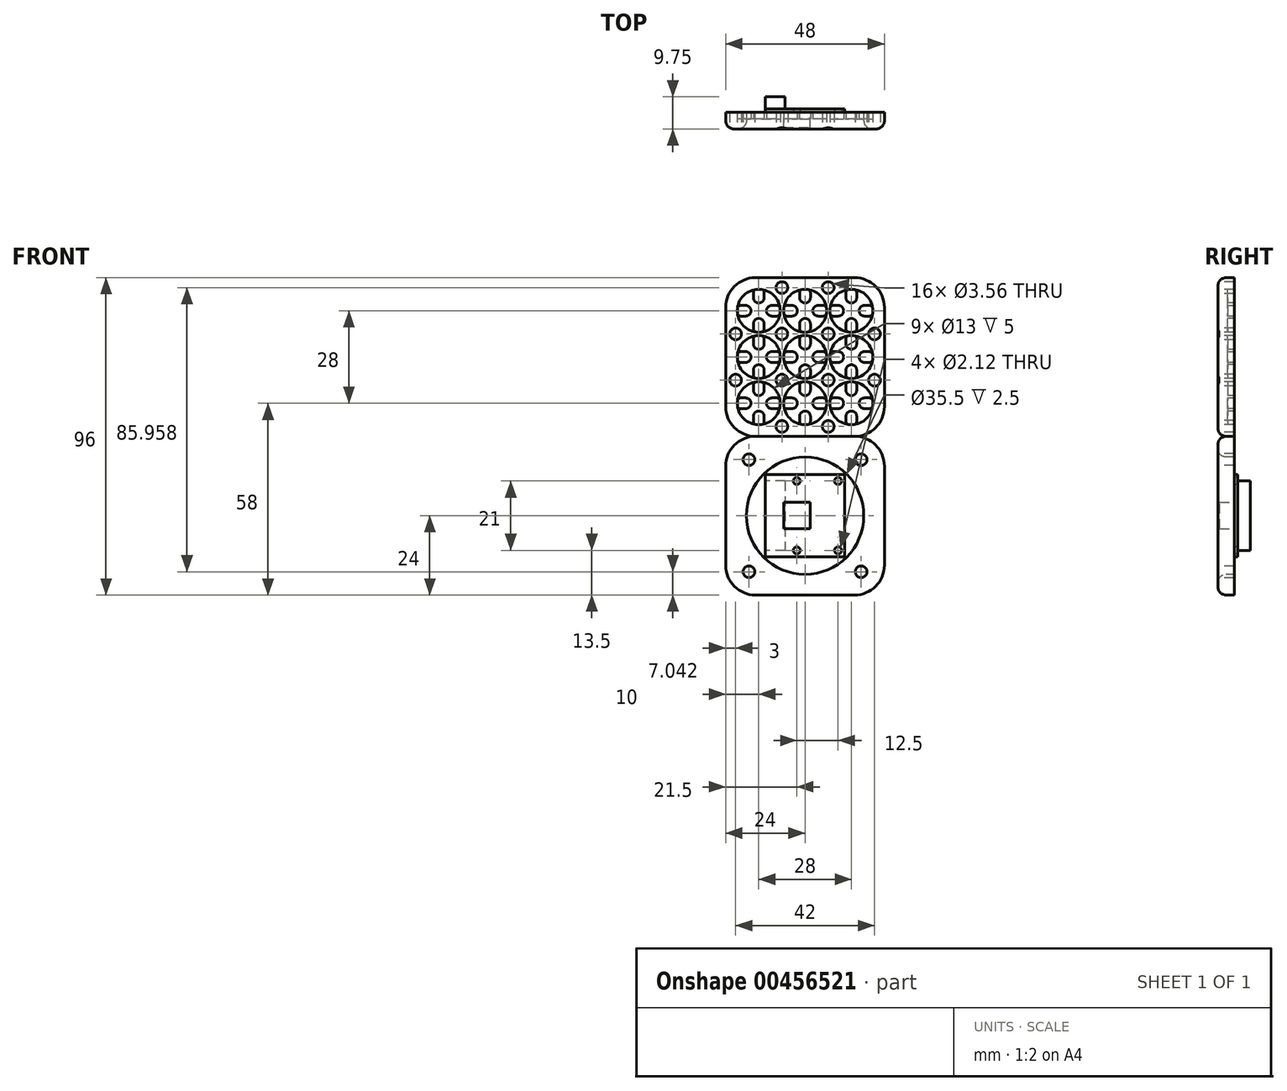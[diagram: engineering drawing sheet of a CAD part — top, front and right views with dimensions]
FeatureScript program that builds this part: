
annotation { "Feature Type Name" : "Feature", "Feature Type Description" : "" }
export const myFeature = defineFeature(function(context is Context, id is Id, definition is map)
    precondition{}
    {
        {
            var Q0;
            Q0=qCreatedBy(makeId("Front.planeOp"),FACE);
            var sketch = newSketch(context, id + "F0", { "sketchPlane" : qUnion([Q0])});
            skCircle(sketch, "E0", {"center": v(0, 0) * mm, "radius": 6.5 * mm});
            skCircle(sketch, "E1", {"center": v(0, 0) * mm, "radius": 7 * mm, "construction": true});
            skLineSegment(sketch, "E2", {"start": v(0, 7) * mm, "end": v(0, 14) * mm, "construction": true});
            skCircle(sketch, "E3", {"center": v(0, 14) * mm, "radius": 7 * mm, "construction": true});
            skCircle(sketch, "E4", {"center": v(0, 14) * mm, "radius": 6.5 * mm});
            skLineSegment(sketch, "E5", {"start": v(0, -7) * mm, "end": v(0, -14) * mm, "construction": true});
            skCircle(sketch, "E6", {"center": v(0, -14) * mm, "radius": 7 * mm, "construction": true});
            skCircle(sketch, "E7", {"center": v(0, -14) * mm, "radius": 6.5 * mm});
            skLineSegment(sketch, "E8", {"start": v(-7, 14) * mm, "end": v(-14, 14) * mm, "construction": true});
            skLineSegment(sketch, "E9", {"start": v(-7, 0) * mm, "end": v(-14, 0) * mm, "construction": true});
            skLineSegment(sketch, "E10", {"start": v(-7, -14) * mm, "end": v(-14, -14) * mm, "construction": true});
            skLineSegment(sketch, "E11", {"start": v(7, 14) * mm, "end": v(14, 14) * mm, "construction": true});
            skLineSegment(sketch, "E12", {"start": v(7, 0) * mm, "end": v(14, 0) * mm, "construction": true});
            skLineSegment(sketch, "E13", {"start": v(7, -14) * mm, "end": v(14, -14) * mm, "construction": true});
            skCircle(sketch, "E14", {"center": v(14, 14) * mm, "radius": 7 * mm, "construction": true});
            skCircle(sketch, "E15", {"center": v(14, 0) * mm, "radius": 7 * mm, "construction": true});
            skCircle(sketch, "E16", {"center": v(14, -14) * mm, "radius": 7 * mm, "construction": true});
            skCircle(sketch, "E17", {"center": v(-14, -14) * mm, "radius": 7 * mm, "construction": true});
            skCircle(sketch, "E18", {"center": v(-14, 0) * mm, "radius": 7 * mm, "construction": true});
            skCircle(sketch, "E19", {"center": v(-14, 14) * mm, "radius": 7 * mm, "construction": true});
            skCircle(sketch, "E20", {"center": v(-14, 14) * mm, "radius": 6.5 * mm});
            skCircle(sketch, "E21", {"center": v(-14, 0) * mm, "radius": 6.5 * mm});
            skCircle(sketch, "E22", {"center": v(-14, -14) * mm, "radius": 6.5 * mm});
            skCircle(sketch, "E23", {"center": v(14, -14) * mm, "radius": 6.5 * mm});
            skCircle(sketch, "E24", {"center": v(14, 0) * mm, "radius": 6.5 * mm});
            skCircle(sketch, "E25", {"center": v(14, 14) * mm, "radius": 6.5 * mm});
            skLineSegment(sketch, "E26", {"start": v(-14, 14) * mm, "end": v(-21, 14) * mm, "construction": true});
            skLineSegment(sketch, "E27", {"start": v(-14, 14) * mm, "end": v(-14, 21) * mm, "construction": true});
            skLineSegment(sketch, "E28", {"start": v(14, -14) * mm, "end": v(14, -21) * mm, "construction": true});
            skLineSegment(sketch, "E29", {"start": v(14, -14) * mm, "end": v(21, -14) * mm, "construction": true});
            skLineSegment(sketch, "E30.rect.bottom", {"start": v(-21, 21) * mm, "end": v(21, 21) * mm, "construction": true});
            skLineSegment(sketch, "E30.rect.top", {"start": v(-12, -21) * mm, "end": v(21, -21) * mm, "construction": true});
            skLineSegment(sketch, "E30.rect.left", {"start": v(-21, 21) * mm, "end": v(-21, -12) * mm, "construction": true});
            skLineSegment(sketch, "E30.rect.right", {"start": v(21, 21) * mm, "end": v(21, -21) * mm, "construction": true});
            skLineSegment(sketch, "E31.0", {"start": v(-24, 15) * mm, "end": v(-24, -15) * mm});
            skLineSegment(sketch, "E31.1", {"start": v(-15, 24) * mm, "end": v(15, 24) * mm});
            skLineSegment(sketch, "E31.2", {"start": v(24, 15) * mm, "end": v(24, -15) * mm});
            skLineSegment(sketch, "E31.3", {"start": v(-15, -24) * mm, "end": v(15, -24) * mm});
            skPoint(sketch, "E32.visualSharp", {"position": v(-24, -24) * mm});
            skArc(sketch, "E32.filletArc", {"start": v(-24, -15) * mm, "mid": v(-21.36, -21.36) * mm, "end": v(-15, -24) * mm});
            skPoint(sketch, "E33.visualSharp", {"position": v(-24, 24) * mm});
            skArc(sketch, "E33.filletArc", {"start": v(-15, 24) * mm, "mid": v(-21.36, 21.36) * mm, "end": v(-24, 15) * mm});
            skPoint(sketch, "E34.visualSharp", {"position": v(24, 24) * mm});
            skArc(sketch, "E34.filletArc", {"start": v(24, 15) * mm, "mid": v(21.36, 21.36) * mm, "end": v(15, 24) * mm});
            skPoint(sketch, "E35.visualSharp", {"position": v(24, -24) * mm});
            skArc(sketch, "E35.filletArc", {"start": v(15, -24) * mm, "mid": v(21.36, -21.36) * mm, "end": v(24, -15) * mm});
            skPoint(sketch, "E36.visualSharp", {"position": v(-21, -21) * mm});
            skArc(sketch, "E36.filletArc", {"start": v(-21, -12) * mm, "mid": v(-18.36, -18.36) * mm, "end": v(-12, -21) * mm, "construction": true});
            skLineSegment(sketch, "E37", {"start": v(7, -14) * mm, "end": v(7, 14) * mm, "construction": true});
            skLineSegment(sketch, "E38", {"start": v(14, -7) * mm, "end": v(-14, -7) * mm, "construction": true});
            skLineSegment(sketch, "E39", {"start": v(-7, -14) * mm, "end": v(-7, 14) * mm, "construction": true});
            skLineSegment(sketch, "E40", {"start": v(14, -7) * mm, "end": v(24, -7) * mm, "construction": true});
            skLineSegment(sketch, "E41", {"start": v(7, -14) * mm, "end": v(7, -24) * mm, "construction": true});
            skLineSegment(sketch, "E42", {"start": v(-7, -14) * mm, "end": v(-7, -24) * mm, "construction": true});
            skLineSegment(sketch, "E43", {"start": v(-14, -7) * mm, "end": v(-24, -7) * mm, "construction": true});
            skLineSegment(sketch, "E44", {"start": v(14, 7) * mm, "end": v(-14, 7) * mm, "construction": true});
            skLineSegment(sketch, "E45", {"start": v(14, 7) * mm, "end": v(24, 7) * mm, "construction": true});
            skLineSegment(sketch, "E46", {"start": v(7, 14) * mm, "end": v(7, 24) * mm, "construction": true});
            skLineSegment(sketch, "E47", {"start": v(-7, 14) * mm, "end": v(-7, 24) * mm, "construction": true});
            skLineSegment(sketch, "E48", {"start": v(-14, 7) * mm, "end": v(-24, 7) * mm, "construction": true});
            skCircle(sketch, "E49", {"center": v(7, -7) * mm, "radius": 1.78 * mm});
            skCircle(sketch, "E50", {"center": v(-7, -7) * mm, "radius": 1.78 * mm});
            skCircle(sketch, "E51", {"center": v(-7, 7) * mm, "radius": 1.78 * mm});
            skCircle(sketch, "E52", {"center": v(7, 7) * mm, "radius": 1.78 * mm});
            skCircle(sketch, "E53", {"center": v(-7, -21) * mm, "radius": 1.78 * mm});
            skCircle(sketch, "E54", {"center": v(7, -21) * mm, "radius": 1.78 * mm});
            skCircle(sketch, "E55", {"center": v(21, -7) * mm, "radius": 1.78 * mm});
            skCircle(sketch, "E56", {"center": v(21, 7) * mm, "radius": 1.78 * mm});
            skCircle(sketch, "E57", {"center": v(7, 21) * mm, "radius": 1.78 * mm});
            skCircle(sketch, "E58", {"center": v(-7, 21) * mm, "radius": 1.78 * mm});
            skCircle(sketch, "E59", {"center": v(-21, 7) * mm, "radius": 1.78 * mm});
            skCircle(sketch, "E60", {"center": v(-21, -7) * mm, "radius": 1.78 * mm});
            skSolve(sketch);
        }
        {
            var Q0;
            Q0=makeQuery(id+"F0.imprint","IMPRINT",FACE,{"disambiguationData":[TD([[makeQuery(id+"F0.imprint","IMPRINT",EDGE,{"derivedFrom":sQuery(id+"F0.wireOp",EDGE,"E0")}),-1.0]])]});
            var Q1;
            Q1=makeQuery(id+"F0.imprint","IMPRINT",FACE,{"disambiguationData":[TD([[makeQuery(id+"F0.imprint","IMPRINT",EDGE,{"derivedFrom":sQuery(id+"F0.wireOp",EDGE,"E21")}),1.0]])]});
            var Q2;
            Q2=makeQuery(id+"F0.imprint","IMPRINT",FACE,{"disambiguationData":[TD([[makeQuery(id+"F0.imprint","IMPRINT",EDGE,{"derivedFrom":sQuery(id+"F0.wireOp",EDGE,"E22")}),1.0]])]});
            var Q3;
            Q3=makeQuery(id+"F0.imprint","IMPRINT",FACE,{"disambiguationData":[TD([[makeQuery(id+"F0.imprint","IMPRINT",EDGE,{"derivedFrom":sQuery(id+"F0.wireOp",EDGE,"E7")}),1.0]])]});
            var Q4;
            Q4=makeQuery(id+"F0.imprint","IMPRINT",FACE,{"disambiguationData":[TD([[makeQuery(id+"F0.imprint","IMPRINT",EDGE,{"derivedFrom":sQuery(id+"F0.wireOp",EDGE,"E0")}),1.0]])]});
            var Q5;
            Q5=makeQuery(id+"F0.imprint","IMPRINT",FACE,{"disambiguationData":[TD([[makeQuery(id+"F0.imprint","IMPRINT",EDGE,{"derivedFrom":sQuery(id+"F0.wireOp",EDGE,"E20")}),1.0]])]});
            var Q6;
            Q6=makeQuery(id+"F0.imprint","IMPRINT",FACE,{"disambiguationData":[TD([[makeQuery(id+"F0.imprint","IMPRINT",EDGE,{"derivedFrom":sQuery(id+"F0.wireOp",EDGE,"E4")}),1.0]])]});
            var Q7;
            Q7=makeQuery(id+"F0.imprint","IMPRINT",FACE,{"disambiguationData":[TD([[makeQuery(id+"F0.imprint","IMPRINT",EDGE,{"derivedFrom":sQuery(id+"F0.wireOp",EDGE,"E25")}),1.0]])]});
            var Q8;
            Q8=makeQuery(id+"F0.imprint","IMPRINT",FACE,{"disambiguationData":[TD([[makeQuery(id+"F0.imprint","IMPRINT",EDGE,{"derivedFrom":sQuery(id+"F0.wireOp",EDGE,"E24")}),1.0]])]});
            var Q9;
            Q9=makeQuery(id+"F0.imprint","IMPRINT",FACE,{"disambiguationData":[TD([[makeQuery(id+"F0.imprint","IMPRINT",EDGE,{"derivedFrom":sQuery(id+"F0.wireOp",EDGE,"E23")}),1.0]])]});
            extrude(context, id + "F1", {"entities" : qUnion([Q0, Q1, Q2, Q3, Q4, Q5, Q6, Q7, Q8, Q9]), "oppositeDirection" : true, "depth" : 5 * mm});
        }
        {
            var Q0;
            Q0=makeQuery(id+"F0.imprint","IMPRINT",FACE,{"disambiguationData":[TD([[makeQuery(id+"F0.imprint","IMPRINT",EDGE,{"derivedFrom":sQuery(id+"F0.wireOp",EDGE,"E22")}),1.0]])]});
            var Q1;
            Q1=makeQuery(id+"F0.imprint","IMPRINT",FACE,{"disambiguationData":[TD([[makeQuery(id+"F0.imprint","IMPRINT",EDGE,{"derivedFrom":sQuery(id+"F0.wireOp",EDGE,"E21")}),1.0]])]});
            var Q2;
            Q2=makeQuery(id+"F0.imprint","IMPRINT",FACE,{"disambiguationData":[TD([[makeQuery(id+"F0.imprint","IMPRINT",EDGE,{"derivedFrom":sQuery(id+"F0.wireOp",EDGE,"E20")}),1.0]])]});
            var Q3;
            Q3=makeQuery(id+"F0.imprint","IMPRINT",FACE,{"disambiguationData":[TD([[makeQuery(id+"F0.imprint","IMPRINT",EDGE,{"derivedFrom":sQuery(id+"F0.wireOp",EDGE,"E4")}),1.0]])]});
            var Q4;
            Q4=makeQuery(id+"F0.imprint","IMPRINT",FACE,{"disambiguationData":[TD([[makeQuery(id+"F0.imprint","IMPRINT",EDGE,{"derivedFrom":sQuery(id+"F0.wireOp",EDGE,"E25")}),1.0]])]});
            var Q5;
            Q5=makeQuery(id+"F0.imprint","IMPRINT",FACE,{"disambiguationData":[TD([[makeQuery(id+"F0.imprint","IMPRINT",EDGE,{"derivedFrom":sQuery(id+"F0.wireOp",EDGE,"E24")}),1.0]])]});
            var Q6;
            Q6=makeQuery(id+"F0.imprint","IMPRINT",FACE,{"disambiguationData":[TD([[makeQuery(id+"F0.imprint","IMPRINT",EDGE,{"derivedFrom":sQuery(id+"F0.wireOp",EDGE,"E23")}),1.0]])]});
            var Q7;
            Q7=makeQuery(id+"F0.imprint","IMPRINT",FACE,{"disambiguationData":[TD([[makeQuery(id+"F0.imprint","IMPRINT",EDGE,{"derivedFrom":sQuery(id+"F0.wireOp",EDGE,"E7")}),1.0]])]});
            var Q8;
            Q8=makeQuery(id+"F0.imprint","IMPRINT",FACE,{"disambiguationData":[TD([[makeQuery(id+"F0.imprint","IMPRINT",EDGE,{"derivedFrom":sQuery(id+"F0.wireOp",EDGE,"E0")}),1.0]])]});
            extrude(context, id + "F2", {"entities" : qUnion([Q0, Q1, Q2, Q3, Q4, Q5, Q6, Q7, Q8]), "operationType" : NewBodyOperationType.REMOVE, "oppositeDirection" : true, "depth" : 3 * mm});
        }
        {
            var Q0;
            Q0=makeQuery(id+"F1.opExtrude","CAP_EDGE",EDGE,{"disambiguationData":[OSD([sQuery(id+"F0.wireOp",EDGE,"E31.3")])],"isStart":true});
            fillet(context, id + "F3", {"entities" : qUnion([Q0]), "radius" : 2.5 * mm, "tangentPropagation" : true, "allowEdgeOverflow" : false});
        }
        {
            var Q0;
            Q0=makeQuery(id+"F0.imprint","IMPRINT",FACE,{"disambiguationData":[TD([[makeQuery(id+"F0.imprint","IMPRINT",EDGE,{"derivedFrom":sQuery(id+"F0.wireOp",EDGE,"E0")}),1.0]])]});
            var sketch = newSketch(context, id + "F4", { "sketchPlane" : qUnion([Q0])});
            skCircle(sketch, "E61.0", {"center": v(-14, 14) * mm, "radius": 6.5 * mm, "construction": true});
            skCircle(sketch, "E62.0", {"center": v(0, 14) * mm, "radius": 6.5 * mm, "construction": true});
            skCircle(sketch, "E63.0", {"center": v(14, 14) * mm, "radius": 6.5 * mm, "construction": true});
            skCircle(sketch, "E64.0", {"center": v(-14, 0) * mm, "radius": 6.5 * mm, "construction": true});
            skCircle(sketch, "E65.0", {"center": v(0, 0) * mm, "radius": 6.5 * mm, "construction": true});
            skCircle(sketch, "E66.0", {"center": v(14, 0) * mm, "radius": 6.5 * mm, "construction": true});
            skCircle(sketch, "E67.0", {"center": v(14, -14) * mm, "radius": 6.5 * mm, "construction": true});
            skCircle(sketch, "E68.0", {"center": v(0, -14) * mm, "radius": 6.5 * mm, "construction": true});
            skCircle(sketch, "E69.0", {"center": v(-14, -14) * mm, "radius": 6.5 * mm, "construction": true});
            skLineSegment(sketch, "E70", {"start": v(0, 0) * mm, "end": v(0, 6.5) * mm, "construction": true});
            skLineSegment(sketch, "E71", {"start": v(0, 0) * mm, "end": v(0, -6.5) * mm, "construction": true});
            skLineSegment(sketch, "E72", {"start": v(0, 0) * mm, "end": v(6.5, 0) * mm, "construction": true});
            skLineSegment(sketch, "E73", {"start": v(0, 0) * mm, "end": v(-6.5, 0) * mm, "construction": true});
            skLineSegment(sketch, "E74", {"start": v(0, 3.25) * mm, "end": v(-3.25, 0) * mm, "construction": true});
            skLineSegment(sketch, "E75", {"start": v(-3.25, 0) * mm, "end": v(0, -3.25) * mm, "construction": true});
            skLineSegment(sketch, "E76", {"start": v(0, -3.25) * mm, "end": v(3.25, 0) * mm, "construction": true});
            skLineSegment(sketch, "E77", {"start": v(3.25, 0) * mm, "end": v(0, 3.25) * mm, "construction": true});
            skLineSegment(sketch, "E78", {"start": v(1.62, 1.63) * mm, "end": v(1.62, 6.3) * mm, "construction": true});
            skLineSegment(sketch, "E79", {"start": v(-1.63, 1.63) * mm, "end": v(-1.63, 6.3) * mm, "construction": true});
            skLineSegment(sketch, "E80", {"start": v(1.62, 1.63) * mm, "end": v(6.3, 1.63) * mm, "construction": true});
            skLineSegment(sketch, "E81", {"start": v(1.63, -1.63) * mm, "end": v(6.3, -1.63) * mm, "construction": true});
            skLineSegment(sketch, "E82", {"start": v(1.63, -1.63) * mm, "end": v(1.63, -6.3) * mm, "construction": true});
            skLineSegment(sketch, "E83", {"start": v(-1.63, -1.62) * mm, "end": v(-1.63, -6.3) * mm, "construction": true});
            skLineSegment(sketch, "E84", {"start": v(-1.63, -1.62) * mm, "end": v(-6.3, -1.62) * mm, "construction": true});
            skLineSegment(sketch, "E85", {"start": v(-1.63, 1.63) * mm, "end": v(-6.3, 1.63) * mm, "construction": true});
            skLineSegment(sketch, "E86", {"start": v(1.63, 3.96) * mm, "end": v(-1.63, 3.96) * mm, "construction": true});
            skLineSegment(sketch, "E87", {"start": v(3.96, 1.63) * mm, "end": v(3.96, -1.63) * mm, "construction": true});
            skLineSegment(sketch, "E88", {"start": v(1.63, -3.96) * mm, "end": v(-1.63, -3.96) * mm, "construction": true});
            skLineSegment(sketch, "E89", {"start": v(-3.96, 1.63) * mm, "end": v(-3.96, -1.62) * mm, "construction": true});
            skCircle(sketch, "E90", {"center": v(3.96, 0) * mm, "radius": 1.63 * mm, "construction": true});
            skCircle(sketch, "E91", {"center": v(0, 3.96) * mm, "radius": 1.63 * mm, "construction": true});
            skCircle(sketch, "E92", {"center": v(-3.96, 0) * mm, "radius": 1.63 * mm, "construction": true});
            skCircle(sketch, "E93", {"center": v(0, -3.96) * mm, "radius": 1.63 * mm, "construction": true});
            skLineSegment(sketch, "E94", {"start": v(6.3, 1.63) * mm, "end": v(3.96, 1.63) * mm});
            skLineSegment(sketch, "E95", {"start": v(6.3, -1.63) * mm, "end": v(3.96, -1.63) * mm});
            skArc(sketch, "E96", {"start": v(6.3, -1.63) * mm, "mid": v(6.5, 0) * mm, "end": v(6.3, 1.63) * mm});
            skArc(sketch, "E97", {"start": v(3.96, 1.63) * mm, "mid": v(2.33, 0) * mm, "end": v(3.96, -1.63) * mm});
            skArc(sketch, "E98", {"start": v(-1.63, 3.96) * mm, "mid": v(0, 2.33) * mm, "end": v(1.63, 3.96) * mm});
            skArc(sketch, "E99", {"start": v(1.63, 6.3) * mm, "mid": v(0, 6.5) * mm, "end": v(-1.63, 6.3) * mm});
            skLineSegment(sketch, "E100", {"start": v(1.63, 6.3) * mm, "end": v(1.63, 3.96) * mm});
            skLineSegment(sketch, "E101", {"start": v(-1.63, 6.3) * mm, "end": v(-1.63, 3.96) * mm});
            skLineSegment(sketch, "E102", {"start": v(1.63, -3.96) * mm, "end": v(1.63, -6.3) * mm});
            skLineSegment(sketch, "E103", {"start": v(-1.63, -6.3) * mm, "end": v(-1.63, -3.96) * mm});
            skLineSegment(sketch, "E104", {"start": v(-3.96, -1.62) * mm, "end": v(-6.3, -1.62) * mm});
            skLineSegment(sketch, "E105", {"start": v(-3.96, 1.63) * mm, "end": v(-6.3, 1.63) * mm});
            skArc(sketch, "E106", {"start": v(-3.96, -1.62) * mm, "mid": v(-2.33, 0) * mm, "end": v(-3.96, 1.63) * mm});
            skArc(sketch, "E107", {"start": v(-6.3, 1.62) * mm, "mid": v(-6.5, 0) * mm, "end": v(-6.3, -1.62) * mm});
            skArc(sketch, "E108", {"start": v(1.63, -3.96) * mm, "mid": v(0, -2.33) * mm, "end": v(-1.63, -3.96) * mm});
            skArc(sketch, "E109", {"start": v(-1.63, -6.3) * mm, "mid": v(0, -6.5) * mm, "end": v(1.63, -6.3) * mm});
            skLineSegment(sketch, "E110.1.0.0", {"start": v(20.3, 1.63) * mm, "end": v(17.96, 1.63) * mm});
            skArc(sketch, "E110.1.0.1", {"start": v(20.3, -1.63) * mm, "mid": v(20.5, 0) * mm, "end": v(20.3, 1.62) * mm});
            skLineSegment(sketch, "E110.1.0.2", {"start": v(20.3, -1.63) * mm, "end": v(17.96, -1.63) * mm});
            skArc(sketch, "E110.1.0.3", {"start": v(17.96, 1.63) * mm, "mid": v(16.33, 0) * mm, "end": v(17.96, -1.63) * mm});
            skArc(sketch, "E110.1.0.4", {"start": v(12.38, 3.96) * mm, "mid": v(14, 2.33) * mm, "end": v(15.62, 3.96) * mm});
            skLineSegment(sketch, "E110.1.0.5", {"start": v(15.62, 6.3) * mm, "end": v(15.62, 3.96) * mm});
            skLineSegment(sketch, "E110.1.0.6", {"start": v(12.38, 6.3) * mm, "end": v(12.38, 3.96) * mm});
            skArc(sketch, "E110.1.0.7", {"start": v(15.62, 6.3) * mm, "mid": v(14, 6.5) * mm, "end": v(12.37, 6.3) * mm});
            skLineSegment(sketch, "E110.1.0.8", {"start": v(10.04, 1.63) * mm, "end": v(7.7, 1.63) * mm});
            skArc(sketch, "E110.1.0.9", {"start": v(10.04, -1.62) * mm, "mid": v(11.67, 0) * mm, "end": v(10.04, 1.63) * mm});
            skLineSegment(sketch, "E110.1.0.10", {"start": v(10.04, -1.62) * mm, "end": v(7.7, -1.62) * mm});
            skArc(sketch, "E110.1.0.11", {"start": v(7.7, 1.62) * mm, "mid": v(7.5, 0) * mm, "end": v(7.7, -1.62) * mm});
            skArc(sketch, "E110.1.0.12", {"start": v(15.62, -3.96) * mm, "mid": v(14, -2.33) * mm, "end": v(12.38, -3.96) * mm});
            skLineSegment(sketch, "E110.1.0.13", {"start": v(15.62, -3.96) * mm, "end": v(15.62, -6.3) * mm});
            skLineSegment(sketch, "E110.1.0.14", {"start": v(12.38, -6.3) * mm, "end": v(12.38, -3.96) * mm});
            skArc(sketch, "E110.1.0.15", {"start": v(12.37, -6.3) * mm, "mid": v(14, -6.5) * mm, "end": v(15.62, -6.3) * mm});
            skLineSegment(sketch, "E110.direction1", {"start": v(3.96, 1.63) * mm, "end": v(17.96, 1.63) * mm, "construction": true});
            skArc(sketch, "E111.1.0.0", {"start": v(-10.04, 1.63) * mm, "mid": v(-11.67, 0) * mm, "end": v(-10.04, -1.63) * mm});
            skLineSegment(sketch, "E111.1.0.1", {"start": v(-7.7, 1.63) * mm, "end": v(-10.04, 1.63) * mm});
            skArc(sketch, "E111.1.0.2", {"start": v(-7.7, -1.63) * mm, "mid": v(-7.5, 0) * mm, "end": v(-7.7, 1.63) * mm});
            skLineSegment(sketch, "E111.1.0.3", {"start": v(-7.7, -1.63) * mm, "end": v(-10.04, -1.63) * mm});
            skArc(sketch, "E111.1.0.4", {"start": v(-15.62, 3.96) * mm, "mid": v(-14, 2.33) * mm, "end": v(-12.38, 3.96) * mm});
            skLineSegment(sketch, "E111.1.0.5", {"start": v(-12.38, 6.3) * mm, "end": v(-12.38, 3.96) * mm});
            skArc(sketch, "E111.1.0.6", {"start": v(-12.38, 6.3) * mm, "mid": v(-14, 6.5) * mm, "end": v(-15.62, 6.3) * mm});
            skLineSegment(sketch, "E111.1.0.7", {"start": v(-15.62, 6.3) * mm, "end": v(-15.62, 3.96) * mm});
            skLineSegment(sketch, "E111.1.0.8", {"start": v(-17.96, 1.63) * mm, "end": v(-20.3, 1.63) * mm});
            skArc(sketch, "E111.1.0.9", {"start": v(-17.96, -1.62) * mm, "mid": v(-16.33, 0) * mm, "end": v(-17.96, 1.63) * mm});
            skLineSegment(sketch, "E111.1.0.10", {"start": v(-17.96, -1.62) * mm, "end": v(-20.3, -1.62) * mm});
            skArc(sketch, "E111.1.0.11", {"start": v(-20.3, 1.62) * mm, "mid": v(-20.5, 0) * mm, "end": v(-20.3, -1.62) * mm});
            skArc(sketch, "E111.1.0.12", {"start": v(-12.38, -3.96) * mm, "mid": v(-14, -2.33) * mm, "end": v(-15.62, -3.96) * mm});
            skLineSegment(sketch, "E111.1.0.13", {"start": v(-12.38, -3.96) * mm, "end": v(-12.38, -6.3) * mm});
            skArc(sketch, "E111.1.0.14", {"start": v(-15.62, -6.3) * mm, "mid": v(-14, -6.5) * mm, "end": v(-12.38, -6.3) * mm});
            skLineSegment(sketch, "E111.1.0.15", {"start": v(-15.62, -6.3) * mm, "end": v(-15.62, -3.96) * mm});
            skLineSegment(sketch, "E111.direction1", {"start": v(3.96, -1.63) * mm, "end": v(-10.04, -1.63) * mm, "construction": true});
            skCircle(sketch, "E112.0", {"center": v(21, 7) * mm, "radius": 1.78 * mm, "construction": true});
            skCircle(sketch, "E113.0", {"center": v(21, -7) * mm, "radius": 1.78 * mm, "construction": true});
            skCircle(sketch, "E114.0", {"center": v(7, 21) * mm, "radius": 1.78 * mm, "construction": true});
            skCircle(sketch, "E115.0", {"center": v(-7, 21) * mm, "radius": 1.78 * mm, "construction": true});
            skCircle(sketch, "E116.0", {"center": v(7, 7) * mm, "radius": 1.78 * mm, "construction": true});
            skCircle(sketch, "E117.0", {"center": v(-7, 7) * mm, "radius": 1.78 * mm, "construction": true});
            skCircle(sketch, "E118.0", {"center": v(-21, 7) * mm, "radius": 1.78 * mm, "construction": true});
            skCircle(sketch, "E119.0", {"center": v(-21, -7) * mm, "radius": 1.78 * mm, "construction": true});
            skCircle(sketch, "E120.0", {"center": v(-7, -7) * mm, "radius": 1.78 * mm, "construction": true});
            skCircle(sketch, "E121.0", {"center": v(7, -7) * mm, "radius": 1.78 * mm, "construction": true});
            skCircle(sketch, "E122.0", {"center": v(7, -21) * mm, "radius": 1.78 * mm, "construction": true});
            skCircle(sketch, "E123.0", {"center": v(-7, -21) * mm, "radius": 1.78 * mm, "construction": true});
            skLineSegment(sketch, "E124", {"start": v(14, -14) * mm, "end": v(-14, -14) * mm, "construction": true});
            skLineSegment(sketch, "E125", {"start": v(14, 14) * mm, "end": v(-14, 14) * mm, "construction": true});
            skLineSegment(sketch, "E126", {"start": v(14, 14) * mm, "end": v(14, -14) * mm, "construction": true});
            skLineSegment(sketch, "E127", {"start": v(-14, -14) * mm, "end": v(-14, 14) * mm, "construction": true});
            skLineSegment(sketch, "E128", {"start": v(21, -7) * mm, "end": v(-21, -7) * mm, "construction": true});
            skLineSegment(sketch, "E129", {"start": v(21, 7) * mm, "end": v(-21, 7) * mm, "construction": true});
            skLineSegment(sketch, "E130", {"start": v(7, 21) * mm, "end": v(7, -21) * mm, "construction": true});
            skLineSegment(sketch, "E131", {"start": v(-7, 21) * mm, "end": v(-7, -21) * mm, "construction": true});
            skArc(sketch, "E132.MirrorCS", {"start": v(7.7, 12.38) * mm, "mid": v(7.5, 14) * mm, "end": v(7.7, 15.62) * mm});
            skLineSegment(sketch, "E133.MirrorCS", {"start": v(10.04, 15.62) * mm, "end": v(7.7, 15.62) * mm});
            skArc(sketch, "E134.MirrorCS", {"start": v(10.04, 15.62) * mm, "mid": v(11.67, 14) * mm, "end": v(10.04, 12.38) * mm});
            skLineSegment(sketch, "E135.MirrorCS", {"start": v(10.04, 12.38) * mm, "end": v(7.7, 12.38) * mm});
            skArc(sketch, "E136.MirrorCS", {"start": v(12.38, 10.04) * mm, "mid": v(14, 11.67) * mm, "end": v(15.62, 10.04) * mm});
            skArc(sketch, "E137.MirrorCS", {"start": v(15.62, 7.7) * mm, "mid": v(14, 7.5) * mm, "end": v(12.37, 7.7) * mm});
            skLineSegment(sketch, "E138.MirrorCS", {"start": v(15.62, 7.7) * mm, "end": v(15.62, 10.04) * mm});
            skLineSegment(sketch, "E139.MirrorCS", {"start": v(12.38, 7.7) * mm, "end": v(12.38, 10.04) * mm});
            skLineSegment(sketch, "E140.MirrorCS", {"start": v(12.38, 20.3) * mm, "end": v(12.38, 17.96) * mm});
            skArc(sketch, "E141.MirrorCS", {"start": v(12.37, 20.3) * mm, "mid": v(14, 20.5) * mm, "end": v(15.62, 20.3) * mm});
            skLineSegment(sketch, "E142.MirrorCS", {"start": v(15.62, 17.96) * mm, "end": v(15.62, 20.3) * mm});
            skArc(sketch, "E143.MirrorCS", {"start": v(15.62, 17.96) * mm, "mid": v(14, 16.33) * mm, "end": v(12.38, 17.96) * mm});
            skArc(sketch, "E144.MirrorCS", {"start": v(17.96, 12.38) * mm, "mid": v(16.33, 14) * mm, "end": v(17.96, 15.62) * mm});
            skLineSegment(sketch, "E145.MirrorCS", {"start": v(20.3, 15.62) * mm, "end": v(17.96, 15.62) * mm});
            skLineSegment(sketch, "E146.MirrorCS", {"start": v(20.3, 12.38) * mm, "end": v(17.96, 12.38) * mm});
            skArc(sketch, "E147.MirrorCS", {"start": v(20.3, 15.62) * mm, "mid": v(20.5, 14) * mm, "end": v(20.3, 12.38) * mm});
            skLineSegment(sketch, "E148.MirrorCS", {"start": v(6.3, 12.38) * mm, "end": v(3.96, 12.38) * mm});
            skArc(sketch, "E149.MirrorCS", {"start": v(3.96, 12.38) * mm, "mid": v(2.33, 14) * mm, "end": v(3.96, 15.62) * mm});
            skArc(sketch, "E150.MirrorCS", {"start": v(6.3, 15.62) * mm, "mid": v(6.5, 14) * mm, "end": v(6.3, 12.38) * mm});
            skLineSegment(sketch, "E151.MirrorCS", {"start": v(6.3, 15.62) * mm, "end": v(3.96, 15.62) * mm});
            skLineSegment(sketch, "E152.MirrorCS", {"start": v(1.63, 7.7) * mm, "end": v(1.63, 10.04) * mm});
            skArc(sketch, "E153.MirrorCS", {"start": v(1.63, 7.7) * mm, "mid": v(0, 7.5) * mm, "end": v(-1.63, 7.7) * mm});
            skLineSegment(sketch, "E154.MirrorCS", {"start": v(-1.63, 7.7) * mm, "end": v(-1.63, 10.04) * mm});
            skArc(sketch, "E155.MirrorCS", {"start": v(-1.63, 10.04) * mm, "mid": v(0, 11.67) * mm, "end": v(1.63, 10.04) * mm});
            skArc(sketch, "E156.MirrorCS", {"start": v(1.63, 17.96) * mm, "mid": v(0, 16.33) * mm, "end": v(-1.63, 17.96) * mm});
            skLineSegment(sketch, "E157.MirrorCS", {"start": v(1.63, 17.96) * mm, "end": v(1.63, 20.3) * mm});
            skLineSegment(sketch, "E158.MirrorCS", {"start": v(-1.63, 20.3) * mm, "end": v(-1.63, 17.96) * mm});
            skArc(sketch, "E159.MirrorCS", {"start": v(-1.63, 20.3) * mm, "mid": v(0, 20.5) * mm, "end": v(1.63, 20.3) * mm});
            skLineSegment(sketch, "E160.MirrorCS", {"start": v(-3.96, 12.38) * mm, "end": v(-6.3, 12.38) * mm});
            skArc(sketch, "E161.MirrorCS", {"start": v(-3.96, 15.62) * mm, "mid": v(-2.33, 14) * mm, "end": v(-3.96, 12.38) * mm});
            skLineSegment(sketch, "E162.MirrorCS", {"start": v(-3.96, 15.62) * mm, "end": v(-6.3, 15.62) * mm});
            skArc(sketch, "E163.MirrorCS", {"start": v(-6.3, 12.38) * mm, "mid": v(-6.5, 14) * mm, "end": v(-6.3, 15.62) * mm});
            skLineSegment(sketch, "E164.MirrorCS", {"start": v(-7.7, 12.38) * mm, "end": v(-10.04, 12.38) * mm});
            skArc(sketch, "E165.MirrorCS", {"start": v(-7.7, 15.62) * mm, "mid": v(-7.5, 14) * mm, "end": v(-7.7, 12.38) * mm});
            skLineSegment(sketch, "E166.MirrorCS", {"start": v(-7.7, 15.62) * mm, "end": v(-10.04, 15.62) * mm});
            skArc(sketch, "E167.MirrorCS", {"start": v(-10.04, 12.38) * mm, "mid": v(-11.67, 14) * mm, "end": v(-10.04, 15.62) * mm});
            skArc(sketch, "E168.MirrorCS", {"start": v(-15.62, 10.04) * mm, "mid": v(-14, 11.67) * mm, "end": v(-12.38, 10.04) * mm});
            skLineSegment(sketch, "E169.MirrorCS", {"start": v(-12.38, 7.7) * mm, "end": v(-12.38, 10.04) * mm});
            skArc(sketch, "E170.MirrorCS", {"start": v(-12.38, 7.7) * mm, "mid": v(-14, 7.5) * mm, "end": v(-15.62, 7.7) * mm});
            skLineSegment(sketch, "E171.MirrorCS", {"start": v(-15.62, 7.7) * mm, "end": v(-15.62, 10.04) * mm});
            skLineSegment(sketch, "E172.MirrorCS", {"start": v(-17.96, 12.38) * mm, "end": v(-20.3, 12.38) * mm});
            skArc(sketch, "E173.MirrorCS", {"start": v(-17.96, 15.62) * mm, "mid": v(-16.33, 14) * mm, "end": v(-17.96, 12.38) * mm});
            skLineSegment(sketch, "E174.MirrorCS", {"start": v(-17.96, 15.62) * mm, "end": v(-20.3, 15.62) * mm});
            skArc(sketch, "E175.MirrorCS", {"start": v(-20.3, 12.38) * mm, "mid": v(-20.5, 14) * mm, "end": v(-20.3, 15.62) * mm});
            skLineSegment(sketch, "E176.MirrorCS", {"start": v(-12.38, 17.96) * mm, "end": v(-12.38, 20.3) * mm});
            skArc(sketch, "E177.MirrorCS", {"start": v(-12.38, 17.96) * mm, "mid": v(-14, 16.33) * mm, "end": v(-15.62, 17.96) * mm});
            skLineSegment(sketch, "E178.MirrorCS", {"start": v(-15.62, 20.3) * mm, "end": v(-15.62, 17.96) * mm});
            skArc(sketch, "E179.MirrorCS", {"start": v(-15.62, 20.3) * mm, "mid": v(-14, 20.5) * mm, "end": v(-12.38, 20.3) * mm});
            skArc(sketch, "E180.MirrorCS", {"start": v(15.62, -20.3) * mm, "mid": v(14, -20.5) * mm, "end": v(12.37, -20.3) * mm});
            skLineSegment(sketch, "E181.MirrorCS", {"start": v(15.62, -20.3) * mm, "end": v(15.62, -17.96) * mm});
            skArc(sketch, "E182.MirrorCS", {"start": v(12.38, -17.96) * mm, "mid": v(14, -16.33) * mm, "end": v(15.62, -17.96) * mm});
            skLineSegment(sketch, "E183.MirrorCS", {"start": v(12.38, -20.3) * mm, "end": v(12.38, -17.96) * mm});
            skLineSegment(sketch, "E184.MirrorCS", {"start": v(20.3, -15.62) * mm, "end": v(17.96, -15.62) * mm});
            skArc(sketch, "E185.MirrorCS", {"start": v(20.3, -12.38) * mm, "mid": v(20.5, -14) * mm, "end": v(20.3, -15.62) * mm});
            skLineSegment(sketch, "E186.MirrorCS", {"start": v(20.3, -12.38) * mm, "end": v(17.96, -12.38) * mm});
            skArc(sketch, "E187.MirrorCS", {"start": v(17.96, -15.62) * mm, "mid": v(16.33, -14) * mm, "end": v(17.96, -12.38) * mm});
            skArc(sketch, "E188.MirrorCS", {"start": v(15.62, -10.04) * mm, "mid": v(14, -11.67) * mm, "end": v(12.38, -10.04) * mm});
            skLineSegment(sketch, "E189.MirrorCS", {"start": v(15.62, -10.04) * mm, "end": v(15.62, -7.7) * mm});
            skArc(sketch, "E190.MirrorCS", {"start": v(12.37, -7.7) * mm, "mid": v(14, -7.5) * mm, "end": v(15.62, -7.7) * mm});
            skLineSegment(sketch, "E191.MirrorCS", {"start": v(12.38, -7.7) * mm, "end": v(12.38, -10.04) * mm});
            skArc(sketch, "E192.MirrorCS", {"start": v(10.04, -12.38) * mm, "mid": v(11.67, -14) * mm, "end": v(10.04, -15.62) * mm});
            skLineSegment(sketch, "E193.MirrorCS", {"start": v(10.04, -15.62) * mm, "end": v(7.7, -15.62) * mm});
            skArc(sketch, "E194.MirrorCS", {"start": v(7.7, -15.62) * mm, "mid": v(7.5, -14) * mm, "end": v(7.7, -12.38) * mm});
            skLineSegment(sketch, "E195.MirrorCS", {"start": v(10.04, -12.38) * mm, "end": v(7.7, -12.38) * mm});
            skArc(sketch, "E196.MirrorCS", {"start": v(6.3, -12.38) * mm, "mid": v(6.5, -14) * mm, "end": v(6.3, -15.62) * mm});
            skLineSegment(sketch, "E197.MirrorCS", {"start": v(6.3, -15.62) * mm, "end": v(3.96, -15.62) * mm});
            skArc(sketch, "E198.MirrorCS", {"start": v(3.96, -15.62) * mm, "mid": v(2.33, -14) * mm, "end": v(3.96, -12.38) * mm});
            skLineSegment(sketch, "E199.MirrorCS", {"start": v(1.63, -20.3) * mm, "end": v(1.63, -17.96) * mm});
            skArc(sketch, "E200.MirrorCS", {"start": v(-1.63, -17.96) * mm, "mid": v(0, -16.33) * mm, "end": v(1.63, -17.96) * mm});
            skLineSegment(sketch, "E201.MirrorCS", {"start": v(-1.63, -20.3) * mm, "end": v(-1.63, -17.96) * mm});
            skArc(sketch, "E202.MirrorCS", {"start": v(1.63, -20.3) * mm, "mid": v(0, -20.5) * mm, "end": v(-1.63, -20.3) * mm});
            skLineSegment(sketch, "E203.MirrorCS", {"start": v(-3.96, -15.62) * mm, "end": v(-6.3, -15.62) * mm});
            skArc(sketch, "E204.MirrorCS", {"start": v(-3.96, -12.38) * mm, "mid": v(-2.33, -14) * mm, "end": v(-3.96, -15.62) * mm});
            skLineSegment(sketch, "E205.MirrorCS", {"start": v(-3.96, -12.38) * mm, "end": v(-6.3, -12.38) * mm});
            skArc(sketch, "E206.MirrorCS", {"start": v(-6.3, -15.62) * mm, "mid": v(-6.5, -14) * mm, "end": v(-6.3, -12.38) * mm});
            skArc(sketch, "E207.MirrorCS", {"start": v(1.63, -10.04) * mm, "mid": v(0, -11.67) * mm, "end": v(-1.63, -10.04) * mm});
            skLineSegment(sketch, "E208.MirrorCS", {"start": v(1.63, -10.04) * mm, "end": v(1.63, -7.7) * mm});
            skLineSegment(sketch, "E209.MirrorCS", {"start": v(-1.63, -7.7) * mm, "end": v(-1.63, -10.04) * mm});
            skArc(sketch, "E210.MirrorCS", {"start": v(-1.63, -7.7) * mm, "mid": v(0, -7.5) * mm, "end": v(1.63, -7.7) * mm});
            skArc(sketch, "E211.MirrorCS", {"start": v(-7.7, -12.38) * mm, "mid": v(-7.5, -14) * mm, "end": v(-7.7, -15.62) * mm});
            skLineSegment(sketch, "E212.MirrorCS", {"start": v(-7.7, -15.62) * mm, "end": v(-10.04, -15.62) * mm});
            skArc(sketch, "E213.MirrorCS", {"start": v(-10.04, -15.62) * mm, "mid": v(-11.67, -14) * mm, "end": v(-10.04, -12.38) * mm});
            skLineSegment(sketch, "E214.MirrorCS", {"start": v(-7.7, -12.38) * mm, "end": v(-10.04, -12.38) * mm});
            skLineSegment(sketch, "E215.MirrorCS", {"start": v(-12.38, -20.3) * mm, "end": v(-12.38, -17.96) * mm});
            skArc(sketch, "E216.MirrorCS", {"start": v(-12.38, -20.3) * mm, "mid": v(-14, -20.5) * mm, "end": v(-15.62, -20.3) * mm});
            skLineSegment(sketch, "E217.MirrorCS", {"start": v(-15.62, -20.3) * mm, "end": v(-15.62, -17.96) * mm});
            skArc(sketch, "E218.MirrorCS", {"start": v(-15.62, -17.96) * mm, "mid": v(-14, -16.33) * mm, "end": v(-12.38, -17.96) * mm});
            skLineSegment(sketch, "E219.MirrorCS", {"start": v(-17.96, -15.62) * mm, "end": v(-20.3, -15.62) * mm});
            skArc(sketch, "E220.MirrorCS", {"start": v(-17.96, -12.38) * mm, "mid": v(-16.33, -14) * mm, "end": v(-17.96, -15.62) * mm});
            skLineSegment(sketch, "E221.MirrorCS", {"start": v(-17.96, -12.38) * mm, "end": v(-20.3, -12.38) * mm});
            skArc(sketch, "E222.MirrorCS", {"start": v(-20.3, -15.62) * mm, "mid": v(-20.5, -14) * mm, "end": v(-20.3, -12.38) * mm});
            skArc(sketch, "E223.MirrorCS", {"start": v(-12.38, -10.04) * mm, "mid": v(-14, -11.67) * mm, "end": v(-15.62, -10.04) * mm});
            skLineSegment(sketch, "E224.MirrorCS", {"start": v(-12.38, -10.04) * mm, "end": v(-12.38, -7.7) * mm});
            skArc(sketch, "E225.MirrorCS", {"start": v(-15.62, -7.7) * mm, "mid": v(-14, -7.5) * mm, "end": v(-12.38, -7.7) * mm});
            skLineSegment(sketch, "E226.MirrorCS", {"start": v(-15.62, -7.7) * mm, "end": v(-15.62, -10.04) * mm});
            skLineSegment(sketch, "E227", {"start": v(6.3, -12.38) * mm, "end": v(3.96, -12.38) * mm});
            skSolve(sketch);
        }
        {
            var Q0;
            Q0=qSketchRegion(id+"F4",true);
            extrude(context, id + "F5", {"entities" : qUnion([Q0]), "operationType" : NewBodyOperationType.REMOVE, "oppositeDirection" : true, "depth" : 25 * mm});
        }
        {
            var Q0;
            Q0=makeQuery(id+"F5.boolean.opBoolean","COPY",EDGE,{"derivedFrom":makeQuery(id+"F5.opExtrude","SWEPT_EDGE",EDGE,{"disambiguationData":[OSD([sQuery(id+"F0.wireOp",EDGE,"E0"),sQuery(id+"F4.wireOp",EDGE,"E95"),sQuery(id+"F4.wireOp",EDGE,"E96")])]})});
            var Q1;
            Q1=makeQuery(id+"F5.boolean.opBoolean","COPY",EDGE,{"derivedFrom":makeQuery(id+"F5.opExtrude","SWEPT_EDGE",EDGE,{"disambiguationData":[OSD([sQuery(id+"F0.wireOp",EDGE,"E0"),sQuery(id+"F4.wireOp",EDGE,"E94"),sQuery(id+"F4.wireOp",EDGE,"E96")])]})});
            var Q2;
            Q2=makeQuery(id+"F5.boolean.opBoolean","COPY",EDGE,{"derivedFrom":makeQuery(id+"F5.opExtrude","SWEPT_EDGE",EDGE,{"disambiguationData":[OSD([sQuery(id+"F0.wireOp",EDGE,"E0"),sQuery(id+"F4.wireOp",EDGE,"E99"),sQuery(id+"F4.wireOp",EDGE,"E100")])]})});
            var Q3;
            Q3=makeQuery(id+"F5.boolean.opBoolean","COPY",EDGE,{"derivedFrom":makeQuery(id+"F5.opExtrude","SWEPT_EDGE",EDGE,{"disambiguationData":[OSD([sQuery(id+"F0.wireOp",EDGE,"E0"),sQuery(id+"F4.wireOp",EDGE,"E99"),sQuery(id+"F4.wireOp",EDGE,"E101")])]})});
            var Q4;
            Q4=makeQuery(id+"F5.boolean.opBoolean","COPY",EDGE,{"derivedFrom":makeQuery(id+"F5.opExtrude","SWEPT_EDGE",EDGE,{"disambiguationData":[OSD([sQuery(id+"F0.wireOp",EDGE,"E0"),sQuery(id+"F4.wireOp",EDGE,"E105"),sQuery(id+"F4.wireOp",EDGE,"E107")])]})});
            var Q5;
            Q5=makeQuery(id+"F5.boolean.opBoolean","COPY",EDGE,{"derivedFrom":makeQuery(id+"F5.opExtrude","SWEPT_EDGE",EDGE,{"disambiguationData":[OSD([sQuery(id+"F0.wireOp",EDGE,"E0"),sQuery(id+"F4.wireOp",EDGE,"E104"),sQuery(id+"F4.wireOp",EDGE,"E107")])]})});
            var Q6;
            Q6=makeQuery(id+"F5.boolean.opBoolean","COPY",EDGE,{"derivedFrom":makeQuery(id+"F5.opExtrude","SWEPT_EDGE",EDGE,{"disambiguationData":[OSD([sQuery(id+"F0.wireOp",EDGE,"E0"),sQuery(id+"F4.wireOp",EDGE,"E103"),sQuery(id+"F4.wireOp",EDGE,"E109")])]})});
            var Q7;
            Q7=makeQuery(id+"F5.boolean.opBoolean","COPY",EDGE,{"derivedFrom":makeQuery(id+"F5.opExtrude","SWEPT_EDGE",EDGE,{"disambiguationData":[OSD([sQuery(id+"F0.wireOp",EDGE,"E0"),sQuery(id+"F4.wireOp",EDGE,"E102"),sQuery(id+"F4.wireOp",EDGE,"E109")])]})});
            var Q8;
            Q8=makeQuery(id+"F5.boolean.opBoolean","COPY",EDGE,{"derivedFrom":makeQuery(id+"F5.opExtrude","SWEPT_EDGE",EDGE,{"disambiguationData":[OSD([sQuery(id+"F4.wireOp",EDGE,"E110.1.0.13"),sQuery(id+"F4.wireOp",EDGE,"E110.1.0.15")])]})});
            var Q9;
            Q9=makeQuery(id+"F5.boolean.opBoolean","COPY",EDGE,{"derivedFrom":makeQuery(id+"F5.opExtrude","SWEPT_EDGE",EDGE,{"disambiguationData":[OSD([sQuery(id+"F4.wireOp",EDGE,"E110.1.0.14"),sQuery(id+"F4.wireOp",EDGE,"E110.1.0.15")])]})});
            var Q10;
            Q10=makeQuery(id+"F5.boolean.opBoolean","COPY",EDGE,{"derivedFrom":makeQuery(id+"F5.opExtrude","SWEPT_EDGE",EDGE,{"disambiguationData":[OSD([sQuery(id+"F4.wireOp",EDGE,"E110.1.0.10"),sQuery(id+"F4.wireOp",EDGE,"E110.1.0.11")])]})});
            var Q11;
            Q11=makeQuery(id+"F5.boolean.opBoolean","COPY",EDGE,{"derivedFrom":makeQuery(id+"F5.opExtrude","SWEPT_EDGE",EDGE,{"disambiguationData":[OSD([sQuery(id+"F4.wireOp",EDGE,"E110.1.0.8"),sQuery(id+"F4.wireOp",EDGE,"E110.1.0.11")])]})});
            var Q12;
            Q12=makeQuery(id+"F5.boolean.opBoolean","COPY",EDGE,{"derivedFrom":makeQuery(id+"F5.opExtrude","SWEPT_EDGE",EDGE,{"disambiguationData":[OSD([sQuery(id+"F4.wireOp",EDGE,"E110.1.0.6"),sQuery(id+"F4.wireOp",EDGE,"E110.1.0.7")])]})});
            var Q13;
            Q13=makeQuery(id+"F5.boolean.opBoolean","COPY",EDGE,{"derivedFrom":makeQuery(id+"F5.opExtrude","SWEPT_EDGE",EDGE,{"disambiguationData":[OSD([sQuery(id+"F4.wireOp",EDGE,"E110.1.0.5"),sQuery(id+"F4.wireOp",EDGE,"E110.1.0.7")])]})});
            var Q14;
            Q14=makeQuery(id+"F5.boolean.opBoolean","COPY",EDGE,{"derivedFrom":makeQuery(id+"F5.opExtrude","SWEPT_EDGE",EDGE,{"disambiguationData":[OSD([sQuery(id+"F4.wireOp",EDGE,"E110.1.0.0"),sQuery(id+"F4.wireOp",EDGE,"E110.1.0.1")])]})});
            var Q15;
            Q15=makeQuery(id+"F5.boolean.opBoolean","COPY",EDGE,{"derivedFrom":makeQuery(id+"F5.opExtrude","SWEPT_EDGE",EDGE,{"disambiguationData":[OSD([sQuery(id+"F4.wireOp",EDGE,"E110.1.0.1"),sQuery(id+"F4.wireOp",EDGE,"E110.1.0.2")])]})});
            var Q16;
            Q16=makeQuery(id+"F5.boolean.opBoolean","COPY",EDGE,{"derivedFrom":makeQuery(id+"F5.opExtrude","SWEPT_EDGE",EDGE,{"disambiguationData":[OSD([sQuery(id+"F4.wireOp",EDGE,"E111.1.0.2"),sQuery(id+"F4.wireOp",EDGE,"E111.1.0.3")])]})});
            var Q17;
            Q17=makeQuery(id+"F5.boolean.opBoolean","COPY",EDGE,{"derivedFrom":makeQuery(id+"F5.opExtrude","SWEPT_EDGE",EDGE,{"disambiguationData":[OSD([sQuery(id+"F4.wireOp",EDGE,"E111.1.0.1"),sQuery(id+"F4.wireOp",EDGE,"E111.1.0.2")])]})});
            var Q18;
            Q18=makeQuery(id+"F5.boolean.opBoolean","COPY",EDGE,{"derivedFrom":makeQuery(id+"F5.opExtrude","SWEPT_EDGE",EDGE,{"disambiguationData":[OSD([sQuery(id+"F4.wireOp",EDGE,"E111.1.0.5"),sQuery(id+"F4.wireOp",EDGE,"E111.1.0.6")])]})});
            var Q19;
            Q19=makeQuery(id+"F5.boolean.opBoolean","COPY",EDGE,{"derivedFrom":makeQuery(id+"F5.opExtrude","SWEPT_EDGE",EDGE,{"disambiguationData":[OSD([sQuery(id+"F4.wireOp",EDGE,"E111.1.0.6"),sQuery(id+"F4.wireOp",EDGE,"E111.1.0.7")])]})});
            var Q20;
            Q20=makeQuery(id+"F5.boolean.opBoolean","COPY",EDGE,{"derivedFrom":makeQuery(id+"F5.opExtrude","SWEPT_EDGE",EDGE,{"disambiguationData":[OSD([sQuery(id+"F4.wireOp",EDGE,"E111.1.0.8"),sQuery(id+"F4.wireOp",EDGE,"E111.1.0.11")])]})});
            var Q21;
            Q21=makeQuery(id+"F5.boolean.opBoolean","COPY",EDGE,{"derivedFrom":makeQuery(id+"F5.opExtrude","SWEPT_EDGE",EDGE,{"disambiguationData":[OSD([sQuery(id+"F4.wireOp",EDGE,"E111.1.0.10"),sQuery(id+"F4.wireOp",EDGE,"E111.1.0.11")])]})});
            var Q22;
            Q22=makeQuery(id+"F5.boolean.opBoolean","COPY",EDGE,{"derivedFrom":makeQuery(id+"F5.opExtrude","SWEPT_EDGE",EDGE,{"disambiguationData":[OSD([sQuery(id+"F4.wireOp",EDGE,"E111.1.0.14"),sQuery(id+"F4.wireOp",EDGE,"E111.1.0.15")])]})});
            var Q23;
            Q23=makeQuery(id+"F5.boolean.opBoolean","COPY",EDGE,{"derivedFrom":makeQuery(id+"F5.opExtrude","SWEPT_EDGE",EDGE,{"disambiguationData":[OSD([sQuery(id+"F4.wireOp",EDGE,"E111.1.0.13"),sQuery(id+"F4.wireOp",EDGE,"E111.1.0.14")])]})});
            var Q24;
            Q24=makeQuery(id+"F5.boolean.opBoolean","COPY",EDGE,{"derivedFrom":makeQuery(id+"F5.opExtrude","SWEPT_EDGE",EDGE,{"disambiguationData":[OSD([sQuery(id+"F4.wireOp",EDGE,"E225.MirrorCS"),sQuery(id+"F4.wireOp",EDGE,"E226.MirrorCS")])]})});
            var Q25;
            Q25=makeQuery(id+"F5.boolean.opBoolean","COPY",EDGE,{"derivedFrom":makeQuery(id+"F5.opExtrude","SWEPT_EDGE",EDGE,{"disambiguationData":[OSD([sQuery(id+"F4.wireOp",EDGE,"E221.MirrorCS"),sQuery(id+"F4.wireOp",EDGE,"E222.MirrorCS")])]})});
            var Q26;
            Q26=makeQuery(id+"F5.boolean.opBoolean","COPY",EDGE,{"derivedFrom":makeQuery(id+"F5.opExtrude","SWEPT_EDGE",EDGE,{"disambiguationData":[OSD([sQuery(id+"F4.wireOp",EDGE,"E224.MirrorCS"),sQuery(id+"F4.wireOp",EDGE,"E225.MirrorCS")])]})});
            var Q27;
            Q27=makeQuery(id+"F5.boolean.opBoolean","COPY",EDGE,{"derivedFrom":makeQuery(id+"F5.opExtrude","SWEPT_EDGE",EDGE,{"disambiguationData":[OSD([sQuery(id+"F4.wireOp",EDGE,"E211.MirrorCS"),sQuery(id+"F4.wireOp",EDGE,"E214.MirrorCS")])]})});
            var Q28;
            Q28=makeQuery(id+"F5.boolean.opBoolean","COPY",EDGE,{"derivedFrom":makeQuery(id+"F5.opExtrude","SWEPT_EDGE",EDGE,{"disambiguationData":[OSD([sQuery(id+"F4.wireOp",EDGE,"E211.MirrorCS"),sQuery(id+"F4.wireOp",EDGE,"E212.MirrorCS")])]})});
            var Q29;
            Q29=makeQuery(id+"F5.boolean.opBoolean","COPY",EDGE,{"derivedFrom":makeQuery(id+"F5.opExtrude","SWEPT_EDGE",EDGE,{"disambiguationData":[OSD([sQuery(id+"F4.wireOp",EDGE,"E216.MirrorCS"),sQuery(id+"F4.wireOp",EDGE,"E215.MirrorCS")])]})});
            var Q30;
            Q30=makeQuery(id+"F5.boolean.opBoolean","COPY",EDGE,{"derivedFrom":makeQuery(id+"F5.opExtrude","SWEPT_EDGE",EDGE,{"disambiguationData":[OSD([sQuery(id+"F4.wireOp",EDGE,"E216.MirrorCS"),sQuery(id+"F4.wireOp",EDGE,"E217.MirrorCS")])]})});
            var Q31;
            Q31=makeQuery(id+"F5.boolean.opBoolean","COPY",EDGE,{"derivedFrom":makeQuery(id+"F5.opExtrude","SWEPT_EDGE",EDGE,{"disambiguationData":[OSD([sQuery(id+"F4.wireOp",EDGE,"E219.MirrorCS"),sQuery(id+"F4.wireOp",EDGE,"E222.MirrorCS")])]})});
            var Q32;
            Q32=makeQuery(id+"F5.boolean.opBoolean","COPY",EDGE,{"derivedFrom":makeQuery(id+"F5.opExtrude","SWEPT_EDGE",EDGE,{"disambiguationData":[OSD([sQuery(id+"F4.wireOp",EDGE,"E199.MirrorCS"),sQuery(id+"F4.wireOp",EDGE,"E202.MirrorCS")])]})});
            var Q33;
            Q33=makeQuery(id+"F5.boolean.opBoolean","COPY",EDGE,{"derivedFrom":makeQuery(id+"F5.opExtrude","SWEPT_EDGE",EDGE,{"disambiguationData":[OSD([sQuery(id+"F4.wireOp",EDGE,"E196.MirrorCS"),sQuery(id+"F4.wireOp",EDGE,"E197.MirrorCS")])]})});
            var Q34;
            Q34=makeQuery(id+"F5.boolean.opBoolean","COPY",EDGE,{"derivedFrom":makeQuery(id+"F5.opExtrude","SWEPT_EDGE",EDGE,{"disambiguationData":[OSD([sQuery(id+"F4.wireOp",EDGE,"E201.MirrorCS"),sQuery(id+"F4.wireOp",EDGE,"E202.MirrorCS")])]})});
            var Q35;
            Q35=makeQuery(id+"F5.boolean.opBoolean","COPY",EDGE,{"derivedFrom":makeQuery(id+"F5.opExtrude","SWEPT_EDGE",EDGE,{"disambiguationData":[OSD([sQuery(id+"F4.wireOp",EDGE,"E203.MirrorCS"),sQuery(id+"F4.wireOp",EDGE,"E206.MirrorCS")])]})});
            var Q36;
            Q36=makeQuery(id+"F5.boolean.opBoolean","COPY",EDGE,{"derivedFrom":makeQuery(id+"F5.opExtrude","SWEPT_EDGE",EDGE,{"disambiguationData":[OSD([sQuery(id+"F4.wireOp",EDGE,"E205.MirrorCS"),sQuery(id+"F4.wireOp",EDGE,"E206.MirrorCS")])]})});
            var Q37;
            Q37=makeQuery(id+"F5.boolean.opBoolean","COPY",EDGE,{"derivedFrom":makeQuery(id+"F5.opExtrude","SWEPT_EDGE",EDGE,{"disambiguationData":[OSD([sQuery(id+"F4.wireOp",EDGE,"E209.MirrorCS"),sQuery(id+"F4.wireOp",EDGE,"E210.MirrorCS")])]})});
            var Q38;
            Q38=makeQuery(id+"F5.boolean.opBoolean","COPY",EDGE,{"derivedFrom":makeQuery(id+"F5.opExtrude","SWEPT_EDGE",EDGE,{"disambiguationData":[OSD([sQuery(id+"F4.wireOp",EDGE,"E208.MirrorCS"),sQuery(id+"F4.wireOp",EDGE,"E210.MirrorCS")])]})});
            var Q39;
            Q39=makeQuery(id+"F5.boolean.opBoolean","COPY",EDGE,{"derivedFrom":makeQuery(id+"F5.opExtrude","SWEPT_EDGE",EDGE,{"disambiguationData":[OSD([sQuery(id+"F4.wireOp",EDGE,"E196.MirrorCS"),sQuery(id+"F4.wireOp",EDGE,"E227")])]})});
            var Q40;
            Q40=makeQuery(id+"F5.boolean.opBoolean","COPY",EDGE,{"derivedFrom":makeQuery(id+"F5.opExtrude","SWEPT_EDGE",EDGE,{"disambiguationData":[OSD([sQuery(id+"F4.wireOp",EDGE,"E189.MirrorCS"),sQuery(id+"F4.wireOp",EDGE,"E190.MirrorCS")])]})});
            var Q41;
            Q41=makeQuery(id+"F5.boolean.opBoolean","COPY",EDGE,{"derivedFrom":makeQuery(id+"F5.opExtrude","SWEPT_EDGE",EDGE,{"disambiguationData":[OSD([sQuery(id+"F4.wireOp",EDGE,"E185.MirrorCS"),sQuery(id+"F4.wireOp",EDGE,"E186.MirrorCS")])]})});
            var Q42;
            Q42=makeQuery(id+"F5.boolean.opBoolean","COPY",EDGE,{"derivedFrom":makeQuery(id+"F5.opExtrude","SWEPT_EDGE",EDGE,{"disambiguationData":[OSD([sQuery(id+"F4.wireOp",EDGE,"E194.MirrorCS"),sQuery(id+"F4.wireOp",EDGE,"E195.MirrorCS")])]})});
            var Q43;
            Q43=makeQuery(id+"F5.boolean.opBoolean","COPY",EDGE,{"derivedFrom":makeQuery(id+"F5.opExtrude","SWEPT_EDGE",EDGE,{"disambiguationData":[OSD([sQuery(id+"F4.wireOp",EDGE,"E190.MirrorCS"),sQuery(id+"F4.wireOp",EDGE,"E191.MirrorCS")])]})});
            var Q44;
            Q44=makeQuery(id+"F5.boolean.opBoolean","COPY",EDGE,{"derivedFrom":makeQuery(id+"F5.opExtrude","SWEPT_EDGE",EDGE,{"disambiguationData":[OSD([sQuery(id+"F4.wireOp",EDGE,"E180.MirrorCS"),sQuery(id+"F4.wireOp",EDGE,"E183.MirrorCS")])]})});
            var Q45;
            Q45=makeQuery(id+"F5.boolean.opBoolean","COPY",EDGE,{"derivedFrom":makeQuery(id+"F5.opExtrude","SWEPT_EDGE",EDGE,{"disambiguationData":[OSD([sQuery(id+"F4.wireOp",EDGE,"E193.MirrorCS"),sQuery(id+"F4.wireOp",EDGE,"E194.MirrorCS")])]})});
            var Q46;
            Q46=makeQuery(id+"F5.boolean.opBoolean","COPY",EDGE,{"derivedFrom":makeQuery(id+"F5.opExtrude","SWEPT_EDGE",EDGE,{"disambiguationData":[OSD([sQuery(id+"F4.wireOp",EDGE,"E180.MirrorCS"),sQuery(id+"F4.wireOp",EDGE,"E181.MirrorCS")])]})});
            var Q47;
            Q47=makeQuery(id+"F5.boolean.opBoolean","COPY",EDGE,{"derivedFrom":makeQuery(id+"F5.opExtrude","SWEPT_EDGE",EDGE,{"disambiguationData":[OSD([sQuery(id+"F4.wireOp",EDGE,"E184.MirrorCS"),sQuery(id+"F4.wireOp",EDGE,"E185.MirrorCS")])]})});
            var Q48;
            Q48=makeQuery(id+"F5.boolean.opBoolean","COPY",EDGE,{"derivedFrom":makeQuery(id+"F5.opExtrude","SWEPT_EDGE",EDGE,{"disambiguationData":[OSD([sQuery(id+"F4.wireOp",EDGE,"E174.MirrorCS"),sQuery(id+"F4.wireOp",EDGE,"E175.MirrorCS")])]})});
            var Q49;
            Q49=makeQuery(id+"F5.boolean.opBoolean","COPY",EDGE,{"derivedFrom":makeQuery(id+"F5.opExtrude","SWEPT_EDGE",EDGE,{"disambiguationData":[OSD([sQuery(id+"F4.wireOp",EDGE,"E178.MirrorCS"),sQuery(id+"F4.wireOp",EDGE,"E179.MirrorCS")])]})});
            var Q50;
            Q50=makeQuery(id+"F5.boolean.opBoolean","COPY",EDGE,{"derivedFrom":makeQuery(id+"F5.opExtrude","SWEPT_EDGE",EDGE,{"disambiguationData":[OSD([sQuery(id+"F4.wireOp",EDGE,"E158.MirrorCS"),sQuery(id+"F4.wireOp",EDGE,"E159.MirrorCS")])]})});
            var Q51;
            Q51=makeQuery(id+"F5.boolean.opBoolean","COPY",EDGE,{"derivedFrom":makeQuery(id+"F5.opExtrude","SWEPT_EDGE",EDGE,{"disambiguationData":[OSD([sQuery(id+"F4.wireOp",EDGE,"E162.MirrorCS"),sQuery(id+"F4.wireOp",EDGE,"E163.MirrorCS")])]})});
            var Q52;
            Q52=makeQuery(id+"F5.boolean.opBoolean","COPY",EDGE,{"derivedFrom":makeQuery(id+"F5.opExtrude","SWEPT_EDGE",EDGE,{"disambiguationData":[OSD([sQuery(id+"F4.wireOp",EDGE,"E132.MirrorCS"),sQuery(id+"F4.wireOp",EDGE,"E133.MirrorCS")])]})});
            var Q53;
            Q53=makeQuery(id+"F5.boolean.opBoolean","COPY",EDGE,{"derivedFrom":makeQuery(id+"F5.opExtrude","SWEPT_EDGE",EDGE,{"disambiguationData":[OSD([sQuery(id+"F4.wireOp",EDGE,"E140.MirrorCS"),sQuery(id+"F4.wireOp",EDGE,"E141.MirrorCS")])]})});
            var Q54;
            Q54=makeQuery(id+"F5.boolean.opBoolean","COPY",EDGE,{"derivedFrom":makeQuery(id+"F5.opExtrude","SWEPT_EDGE",EDGE,{"disambiguationData":[OSD([sQuery(id+"F4.wireOp",EDGE,"E172.MirrorCS"),sQuery(id+"F4.wireOp",EDGE,"E175.MirrorCS")])]})});
            var Q55;
            Q55=makeQuery(id+"F5.boolean.opBoolean","COPY",EDGE,{"derivedFrom":makeQuery(id+"F5.opExtrude","SWEPT_EDGE",EDGE,{"disambiguationData":[OSD([sQuery(id+"F4.wireOp",EDGE,"E170.MirrorCS"),sQuery(id+"F4.wireOp",EDGE,"E171.MirrorCS")])]})});
            var Q56;
            Q56=makeQuery(id+"F5.boolean.opBoolean","COPY",EDGE,{"derivedFrom":makeQuery(id+"F5.opExtrude","SWEPT_EDGE",EDGE,{"disambiguationData":[OSD([sQuery(id+"F4.wireOp",EDGE,"E160.MirrorCS"),sQuery(id+"F4.wireOp",EDGE,"E163.MirrorCS")])]})});
            var Q57;
            Q57=makeQuery(id+"F5.boolean.opBoolean","COPY",EDGE,{"derivedFrom":makeQuery(id+"F5.opExtrude","SWEPT_EDGE",EDGE,{"disambiguationData":[OSD([sQuery(id+"F4.wireOp",EDGE,"E153.MirrorCS"),sQuery(id+"F4.wireOp",EDGE,"E154.MirrorCS")])]})});
            var Q58;
            Q58=makeQuery(id+"F5.boolean.opBoolean","COPY",EDGE,{"derivedFrom":makeQuery(id+"F5.opExtrude","SWEPT_EDGE",EDGE,{"disambiguationData":[OSD([sQuery(id+"F4.wireOp",EDGE,"E132.MirrorCS"),sQuery(id+"F4.wireOp",EDGE,"E135.MirrorCS")])]})});
            var Q59;
            Q59=makeQuery(id+"F5.boolean.opBoolean","COPY",EDGE,{"derivedFrom":makeQuery(id+"F5.opExtrude","SWEPT_EDGE",EDGE,{"disambiguationData":[OSD([sQuery(id+"F4.wireOp",EDGE,"E137.MirrorCS"),sQuery(id+"F4.wireOp",EDGE,"E139.MirrorCS")])]})});
            var Q60;
            Q60=makeQuery(id+"F5.boolean.opBoolean","COPY",EDGE,{"derivedFrom":makeQuery(id+"F5.opExtrude","SWEPT_EDGE",EDGE,{"disambiguationData":[OSD([sQuery(id+"F4.wireOp",EDGE,"E169.MirrorCS"),sQuery(id+"F4.wireOp",EDGE,"E170.MirrorCS")])]})});
            var Q61;
            Q61=makeQuery(id+"F5.boolean.opBoolean","COPY",EDGE,{"derivedFrom":makeQuery(id+"F5.opExtrude","SWEPT_EDGE",EDGE,{"disambiguationData":[OSD([sQuery(id+"F4.wireOp",EDGE,"E164.MirrorCS"),sQuery(id+"F4.wireOp",EDGE,"E165.MirrorCS")])]})});
            var Q62;
            Q62=makeQuery(id+"F5.boolean.opBoolean","COPY",EDGE,{"derivedFrom":makeQuery(id+"F5.opExtrude","SWEPT_EDGE",EDGE,{"disambiguationData":[OSD([sQuery(id+"F4.wireOp",EDGE,"E152.MirrorCS"),sQuery(id+"F4.wireOp",EDGE,"E153.MirrorCS")])]})});
            var Q63;
            Q63=makeQuery(id+"F5.boolean.opBoolean","COPY",EDGE,{"derivedFrom":makeQuery(id+"F5.opExtrude","SWEPT_EDGE",EDGE,{"disambiguationData":[OSD([sQuery(id+"F4.wireOp",EDGE,"E148.MirrorCS"),sQuery(id+"F4.wireOp",EDGE,"E150.MirrorCS")])]})});
            var Q64;
            Q64=makeQuery(id+"F5.boolean.opBoolean","COPY",EDGE,{"derivedFrom":makeQuery(id+"F5.opExtrude","SWEPT_EDGE",EDGE,{"disambiguationData":[OSD([sQuery(id+"F4.wireOp",EDGE,"E137.MirrorCS"),sQuery(id+"F4.wireOp",EDGE,"E138.MirrorCS")])]})});
            var Q65;
            Q65=makeQuery(id+"F5.boolean.opBoolean","COPY",EDGE,{"derivedFrom":makeQuery(id+"F5.opExtrude","SWEPT_EDGE",EDGE,{"disambiguationData":[OSD([sQuery(id+"F4.wireOp",EDGE,"E146.MirrorCS"),sQuery(id+"F4.wireOp",EDGE,"E147.MirrorCS")])]})});
            var Q66;
            Q66=makeQuery(id+"F5.boolean.opBoolean","COPY",EDGE,{"derivedFrom":makeQuery(id+"F5.opExtrude","SWEPT_EDGE",EDGE,{"disambiguationData":[OSD([sQuery(id+"F4.wireOp",EDGE,"E176.MirrorCS"),sQuery(id+"F4.wireOp",EDGE,"E179.MirrorCS")])]})});
            var Q67;
            Q67=makeQuery(id+"F5.boolean.opBoolean","COPY",EDGE,{"derivedFrom":makeQuery(id+"F5.opExtrude","SWEPT_EDGE",EDGE,{"disambiguationData":[OSD([sQuery(id+"F4.wireOp",EDGE,"E165.MirrorCS"),sQuery(id+"F4.wireOp",EDGE,"E166.MirrorCS")])]})});
            var Q68;
            Q68=makeQuery(id+"F5.boolean.opBoolean","COPY",EDGE,{"derivedFrom":makeQuery(id+"F5.opExtrude","SWEPT_EDGE",EDGE,{"disambiguationData":[OSD([sQuery(id+"F4.wireOp",EDGE,"E157.MirrorCS"),sQuery(id+"F4.wireOp",EDGE,"E159.MirrorCS")])]})});
            var Q69;
            Q69=makeQuery(id+"F5.boolean.opBoolean","COPY",EDGE,{"derivedFrom":makeQuery(id+"F5.opExtrude","SWEPT_EDGE",EDGE,{"disambiguationData":[OSD([sQuery(id+"F4.wireOp",EDGE,"E150.MirrorCS"),sQuery(id+"F4.wireOp",EDGE,"E151.MirrorCS")])]})});
            var Q70;
            Q70=makeQuery(id+"F5.boolean.opBoolean","COPY",EDGE,{"derivedFrom":makeQuery(id+"F5.opExtrude","SWEPT_EDGE",EDGE,{"disambiguationData":[OSD([sQuery(id+"F4.wireOp",EDGE,"E141.MirrorCS"),sQuery(id+"F4.wireOp",EDGE,"E142.MirrorCS")])]})});
            var Q71;
            Q71=makeQuery(id+"F5.boolean.opBoolean","COPY",EDGE,{"derivedFrom":makeQuery(id+"F5.opExtrude","SWEPT_EDGE",EDGE,{"disambiguationData":[OSD([sQuery(id+"F4.wireOp",EDGE,"E145.MirrorCS"),sQuery(id+"F4.wireOp",EDGE,"E147.MirrorCS")])]})});
            fillet(context, id + "F6", {"entities" : qUnion([Q0, Q1, Q2, Q3, Q4, Q5, Q6, Q7, Q8, Q9, Q10, Q11, Q12, Q13, Q14, Q15, Q16, Q17, Q18, Q19, Q20, Q21, Q22, Q23, Q24, Q25, Q26, Q27, Q28, Q29, Q30, Q31, Q32, Q33, Q34, Q35, Q36, Q37, Q38, Q39, Q40, Q41, Q42, Q43, Q44, Q45, Q46, Q47, Q48, Q49, Q50, Q51, Q52, Q53, Q54, Q55, Q56, Q57, Q58, Q59, Q60, Q61, Q62, Q63, Q64, Q65, Q66, Q67, Q68, Q69, Q70, Q71]), "radius" : 1 * mm, "tangentPropagation" : true, "allowEdgeOverflow" : false});
        }
        {
            var Q0;
            Q0=makeQuery(id+"F1.opExtrude","CAP_FACE",FACE,{"disambiguationData":[OSD([sQuery(id+"F0.wireOp",EDGE,"E31.0"),sQuery(id+"F0.wireOp",EDGE,"E31.1"),sQuery(id+"F0.wireOp",EDGE,"E31.2"),sQuery(id+"F0.wireOp",EDGE,"E31.3"),sQuery(id+"F0.wireOp",EDGE,"E32.filletArc"),sQuery(id+"F0.wireOp",EDGE,"E33.filletArc"),sQuery(id+"F0.wireOp",EDGE,"E34.filletArc"),sQuery(id+"F0.wireOp",EDGE,"E35.filletArc"),sQuery(id+"F0.wireOp",EDGE,"E49"),sQuery(id+"F0.wireOp",EDGE,"E50"),sQuery(id+"F0.wireOp",EDGE,"E51"),sQuery(id+"F0.wireOp",EDGE,"E52"),sQuery(id+"F0.wireOp",EDGE,"E53"),sQuery(id+"F0.wireOp",EDGE,"E54"),sQuery(id+"F0.wireOp",EDGE,"E55"),sQuery(id+"F0.wireOp",EDGE,"E56"),sQuery(id+"F0.wireOp",EDGE,"E57"),sQuery(id+"F0.wireOp",EDGE,"E58"),sQuery(id+"F0.wireOp",EDGE,"E59"),sQuery(id+"F0.wireOp",EDGE,"E60")])],"isStart":true});
            var sketch = newSketch(context, id + "F7", { "sketchPlane" : qUnion([Q0])});
            skLineSegment(sketch, "E228.0", {"start": v(-15, 24) * mm, "end": v(15, 24) * mm, "construction": true});
            skLineSegment(sketch, "E229.0", {"start": v(-15, -24) * mm, "end": v(15, -24) * mm, "construction": true});
            skLineSegment(sketch, "E230.0", {"start": v(-24, -15) * mm, "end": v(-24, 15) * mm, "construction": true});
            skLineSegment(sketch, "E231.0", {"start": v(24, 15) * mm, "end": v(24, -15) * mm, "construction": true});
            skArc(sketch, "E232.0", {"start": v(-24, 15) * mm, "mid": v(-21.36, 21.36) * mm, "end": v(-15, 24) * mm, "construction": true});
            skArc(sketch, "E233.0", {"start": v(-15, -24) * mm, "mid": v(-21.36, -21.36) * mm, "end": v(-24, -15) * mm, "construction": true});
            skArc(sketch, "E234.0", {"start": v(24, -15) * mm, "mid": v(21.36, -21.36) * mm, "end": v(15, -24) * mm, "construction": true});
            skArc(sketch, "E235.0", {"start": v(15, 24) * mm, "mid": v(21.36, 21.36) * mm, "end": v(24, 15) * mm, "construction": true});
            skLineSegment(sketch, "E236", {"start": v(0, 0) * mm, "end": v(0, -24) * mm, "construction": true});
            skLineSegment(sketch, "E237", {"start": v(0, -24) * mm, "end": v(0, -48) * mm, "construction": true});
            skLineSegment(sketch, "E238", {"start": v(0, -48) * mm, "end": v(0, -72) * mm, "construction": true});
            skLineSegment(sketch, "E239", {"start": v(-24, -15) * mm, "end": v(-24, -24) * mm, "construction": true});
            skLineSegment(sketch, "E240", {"start": v(-24, -24) * mm, "end": v(-15, -24) * mm, "construction": true});
            skLineSegment(sketch, "E241", {"start": v(24, -15) * mm, "end": v(24, -24) * mm, "construction": true});
            skLineSegment(sketch, "E242", {"start": v(24, -24) * mm, "end": v(15, -24) * mm, "construction": true});
            skLineSegment(sketch, "E243", {"start": v(24, -24) * mm, "end": v(24, -72) * mm, "construction": true});
            skLineSegment(sketch, "E244", {"start": v(24, -72) * mm, "end": v(0, -72) * mm, "construction": true});
            skLineSegment(sketch, "E245", {"start": v(0, -72) * mm, "end": v(-24, -72) * mm, "construction": true});
            skLineSegment(sketch, "E246", {"start": v(-24, -72) * mm, "end": v(-24, -24) * mm, "construction": true});
            skLineSegment(sketch, "E247", {"start": v(0, -48) * mm, "end": v(-24, -48) * mm, "construction": true});
            skLineSegment(sketch, "E248", {"start": v(0, -48) * mm, "end": v(24, -48) * mm, "construction": true});
            skCircle(sketch, "E249", {"center": v(0, -48) * mm, "radius": 17.75 * mm});
            skCircle(sketch, "E250", {"center": v(0, -48) * mm, "radius": 24 * mm, "construction": true});
            skLineSegment(sketch, "E251.bottom", {"start": v(15, -24) * mm, "end": v(-15, -24) * mm});
            skLineSegment(sketch, "E251.top", {"start": v(15, -72) * mm, "end": v(-15, -72) * mm});
            skLineSegment(sketch, "E251.left", {"start": v(24, -33) * mm, "end": v(24, -63) * mm});
            skLineSegment(sketch, "E251.right", {"start": v(-24, -33) * mm, "end": v(-24, -63) * mm});
            skPoint(sketch, "E252.visualSharp", {"position": v(-24, -72) * mm});
            skArc(sketch, "E252.filletArc", {"start": v(-24, -63) * mm, "mid": v(-21.36, -69.36) * mm, "end": v(-15, -72) * mm});
            skPoint(sketch, "E253.visualSharp", {"position": v(-24, -24) * mm});
            skArc(sketch, "E253.filletArc", {"start": v(-15, -24) * mm, "mid": v(-21.36, -26.64) * mm, "end": v(-24, -33) * mm});
            skPoint(sketch, "E254.visualSharp", {"position": v(24, -72) * mm});
            skArc(sketch, "E254.filletArc", {"start": v(15, -72) * mm, "mid": v(21.36, -69.36) * mm, "end": v(24, -63) * mm});
            skPoint(sketch, "E255.visualSharp", {"position": v(24, -24) * mm});
            skArc(sketch, "E255.filletArc", {"start": v(24, -33) * mm, "mid": v(21.36, -26.64) * mm, "end": v(15, -24) * mm});
            skSolve(sketch);
        }
        {
            var Q0;
            Q0=makeQuery(id+"F7.imprint","IMPRINT",FACE,{"disambiguationData":[TD([[makeQuery(id+"F7.imprint","IMPRINT",EDGE,{"derivedFrom":sQuery(id+"F7.wireOp",EDGE,"E249")}),-1.0]])]});
            var Q1;
            Q1=makeQuery(id+"F1.opExtrude","CAP_FACE",FACE,{"disambiguationData":[OSD([sQuery(id+"F0.wireOp",EDGE,"E31.0"),sQuery(id+"F0.wireOp",EDGE,"E31.1"),sQuery(id+"F0.wireOp",EDGE,"E31.2"),sQuery(id+"F0.wireOp",EDGE,"E31.3"),sQuery(id+"F0.wireOp",EDGE,"E32.filletArc"),sQuery(id+"F0.wireOp",EDGE,"E33.filletArc"),sQuery(id+"F0.wireOp",EDGE,"E34.filletArc"),sQuery(id+"F0.wireOp",EDGE,"E35.filletArc"),sQuery(id+"F0.wireOp",EDGE,"E49"),sQuery(id+"F0.wireOp",EDGE,"E50"),sQuery(id+"F0.wireOp",EDGE,"E51"),sQuery(id+"F0.wireOp",EDGE,"E52"),sQuery(id+"F0.wireOp",EDGE,"E53"),sQuery(id+"F0.wireOp",EDGE,"E54"),sQuery(id+"F0.wireOp",EDGE,"E55"),sQuery(id+"F0.wireOp",EDGE,"E56"),sQuery(id+"F0.wireOp",EDGE,"E57"),sQuery(id+"F0.wireOp",EDGE,"E58"),sQuery(id+"F0.wireOp",EDGE,"E59"),sQuery(id+"F0.wireOp",EDGE,"E60")])],"isStart":false});
            extrude(context, id + "F8", {"entities" : qUnion([Q0]), "endBound" : BoundingType.UP_TO_SURFACE, "oppositeDirection" : true, "endBoundEntityFace" : qUnion([Q1]), "depth" : 25 * mm});
        }
        {
            var Q0;
            Q0=makeQuery(id+"F8.opExtrude","CAP_EDGE",EDGE,{"disambiguationData":[OSD([sQuery(id+"F7.wireOp",EDGE,"E251.right")])],"isStart":true});
            var Q1;
            Q1=makeQuery(id+"F8.opExtrude","CAP_EDGE",EDGE,{"disambiguationData":[OSD([sQuery(id+"F7.wireOp",EDGE,"E249")])],"isStart":true});
            fillet(context, id + "F9", {"entities" : qUnion([Q0, Q1]), "radius" : 2.5 * mm, "tangentPropagation" : true, "allowEdgeOverflow" : false});
        }
        {
            var Q0;
            Q0=makeQuery(id+"F8.opExtrude","CAP_FACE",FACE,{"disambiguationData":[OSD([sQuery(id+"F7.wireOp",EDGE,"E249"),sQuery(id+"F7.wireOp",EDGE,"E251.bottom"),sQuery(id+"F7.wireOp",EDGE,"E251.top"),sQuery(id+"F7.wireOp",EDGE,"E251.left"),sQuery(id+"F7.wireOp",EDGE,"E251.right"),sQuery(id+"F7.wireOp",EDGE,"E252.filletArc"),sQuery(id+"F7.wireOp",EDGE,"E253.filletArc"),sQuery(id+"F7.wireOp",EDGE,"E254.filletArc"),sQuery(id+"F7.wireOp",EDGE,"E255.filletArc")])],"isStart":true});
            var sketch = newSketch(context, id + "F10", { "sketchPlane" : qUnion([Q0])});
            skArc(sketch, "E256.0", {"start": v(-24, -33) * mm, "mid": v(-21.36, -26.64) * mm, "end": v(-15, -24) * mm, "construction": true});
            skLineSegment(sketch, "E257.0", {"start": v(-24, -63) * mm, "end": v(-24, -33) * mm, "construction": true});
            skArc(sketch, "E258.0", {"start": v(-15, -72) * mm, "mid": v(-21.36, -69.36) * mm, "end": v(-24, -63) * mm, "construction": true});
            skLineSegment(sketch, "E259.0", {"start": v(15, -72) * mm, "end": v(-15, -72) * mm, "construction": true});
            skArc(sketch, "E260.0", {"start": v(24, -63) * mm, "mid": v(21.36, -69.36) * mm, "end": v(15, -72) * mm, "construction": true});
            skLineSegment(sketch, "E261.0", {"start": v(24, -63) * mm, "end": v(24, -33) * mm, "construction": true});
            skArc(sketch, "E262.0", {"start": v(15, -24) * mm, "mid": v(21.36, -26.64) * mm, "end": v(24, -33) * mm, "construction": true});
            skLineSegment(sketch, "E263.0", {"start": v(-15, -24) * mm, "end": v(15, -24) * mm, "construction": true});
            skCircle(sketch, "E264.0", {"center": v(0, -48) * mm, "radius": 17.75 * mm, "construction": true});
            skLineSegment(sketch, "E265", {"start": v(0, -48) * mm, "end": v(-21.36, -26.64) * mm, "construction": true});
            skLineSegment(sketch, "E266", {"start": v(0, -48) * mm, "end": v(21.36, -26.64) * mm, "construction": true});
            skLineSegment(sketch, "E267", {"start": v(0, -48) * mm, "end": v(-21.36, -69.36) * mm, "construction": true});
            skLineSegment(sketch, "E268", {"start": v(0, -48) * mm, "end": v(21.36, -69.36) * mm, "construction": true});
            skLineSegment(sketch, "E269", {"start": v(12.55, -60.55) * mm, "end": v(21.36, -69.36) * mm, "construction": true});
            skLineSegment(sketch, "E270", {"start": v(-12.55, -60.55) * mm, "end": v(-21.36, -69.36) * mm, "construction": true});
            skLineSegment(sketch, "E271", {"start": v(-21.36, -26.64) * mm, "end": v(-12.55, -35.45) * mm, "construction": true});
            skLineSegment(sketch, "E272", {"start": v(21.36, -26.64) * mm, "end": v(12.55, -35.45) * mm, "construction": true});
            skCircle(sketch, "E273", {"center": v(16.96, -31.04) * mm, "radius": 1.78 * mm});
            skCircle(sketch, "E274", {"center": v(16.96, -64.96) * mm, "radius": 1.78 * mm});
            skCircle(sketch, "E275", {"center": v(-16.96, -64.96) * mm, "radius": 1.78 * mm});
            skCircle(sketch, "E276", {"center": v(-16.96, -31.04) * mm, "radius": 1.78 * mm});
            skCircle(sketch, "E277.0", {"center": v(-7, -7) * mm, "radius": 1.78 * mm, "construction": true});
            skSolve(sketch);
        }
        {
            var Q0;
            Q0=qSketchRegion(id+"F10",true);
            extrude(context, id + "F11", {"entities" : qUnion([Q0]), "operationType" : NewBodyOperationType.REMOVE, "oppositeDirection" : true, "depth" : 25 * mm});
        }
        {
            var Q0;
            Q0=makeQuery(id+"F8.opExtrude","CAP_FACE",FACE,{"disambiguationData":[OSD([sQuery(id+"F7.wireOp",EDGE,"E249"),sQuery(id+"F7.wireOp",EDGE,"E251.bottom"),sQuery(id+"F7.wireOp",EDGE,"E251.top"),sQuery(id+"F7.wireOp",EDGE,"E251.left"),sQuery(id+"F7.wireOp",EDGE,"E251.right"),sQuery(id+"F7.wireOp",EDGE,"E252.filletArc"),sQuery(id+"F7.wireOp",EDGE,"E253.filletArc"),sQuery(id+"F7.wireOp",EDGE,"E254.filletArc"),sQuery(id+"F7.wireOp",EDGE,"E255.filletArc")])],"isStart":false});
            var sketch = newSketch(context, id + "F12", { "sketchPlane" : qUnion([Q0])});
            skLineSegment(sketch, "E278.0", {"start": v(15, -24) * mm, "end": v(-15, -24) * mm, "construction": true});
            skArc(sketch, "E279.0", {"start": v(24, -33) * mm, "mid": v(21.36, -26.64) * mm, "end": v(15, -24) * mm, "construction": true});
            skLineSegment(sketch, "E280.0", {"start": v(24, -63) * mm, "end": v(24, -33) * mm, "construction": true});
            skArc(sketch, "E281.0", {"start": v(15, -72) * mm, "mid": v(21.36, -69.36) * mm, "end": v(24, -63) * mm, "construction": true});
            skLineSegment(sketch, "E282.0", {"start": v(15, -72) * mm, "end": v(-15, -72) * mm, "construction": true});
            skArc(sketch, "E283.0", {"start": v(-24, -63) * mm, "mid": v(-21.36, -69.36) * mm, "end": v(-15, -72) * mm, "construction": true});
            skLineSegment(sketch, "E284.0", {"start": v(-24, -33) * mm, "end": v(-24, -63) * mm, "construction": true});
            skArc(sketch, "E285.0", {"start": v(-15, -24) * mm, "mid": v(-21.36, -26.64) * mm, "end": v(-24, -33) * mm, "construction": true});
            skLineSegment(sketch, "E286", {"start": v(0, -24) * mm, "end": v(0, -72) * mm, "construction": true});
            skLineSegment(sketch, "E287", {"start": v(24, -48) * mm, "end": v(0, -48) * mm, "construction": true});
            skLineSegment(sketch, "E288", {"start": v(0, -48) * mm, "end": v(-24, -48) * mm, "construction": true});
            skPoint(sketch, "E289.rect.middle", {"position": v(0, -48) * mm});
            skLineSegment(sketch, "E290", {"start": v(-5.79, -48) * mm, "end": v(-5.79, -60.5) * mm, "construction": true});
            skLineSegment(sketch, "E291.top", {"start": v(0, -60.5) * mm, "end": v(-12, -60.5) * mm});
            skLineSegment(sketch, "E291.left", {"start": v(0, -48) * mm, "end": v(0, -60.5) * mm, "construction": true});
            skLineSegment(sketch, "E291.right", {"start": v(-12, -48) * mm, "end": v(-12, -60.5) * mm});
            skLineSegment(sketch, "E292", {"start": v(-5.79, -48) * mm, "end": v(-5.79, -35.5) * mm, "construction": true});
            skLineSegment(sketch, "E293.top", {"start": v(-12, -35.5) * mm, "end": v(0, -35.5) * mm});
            skLineSegment(sketch, "E293.left", {"start": v(-12, -48) * mm, "end": v(-12, -35.5) * mm});
            skLineSegment(sketch, "E293.right", {"start": v(0, -48) * mm, "end": v(0, -35.5) * mm, "construction": true});
            skLineSegment(sketch, "E294.bottom", {"start": v(0, -60.5) * mm, "end": v(12, -60.5) * mm});
            skLineSegment(sketch, "E294.right", {"start": v(12, -60.5) * mm, "end": v(12, -48) * mm});
            skLineSegment(sketch, "E295.bottom", {"start": v(0, -35.5) * mm, "end": v(12, -35.5) * mm});
            skLineSegment(sketch, "E295.top", {"start": v(0, -48) * mm, "end": v(12, -48) * mm, "construction": true});
            skLineSegment(sketch, "E295.right", {"start": v(12, -35.5) * mm, "end": v(12, -48) * mm});
            skPoint(sketch, "E296", {"position": v(-10, -37.5) * mm});
            skLineSegment(sketch, "E297", {"start": v(-10, -37.5) * mm, "end": v(-10, -58.5) * mm, "construction": true});
            skLineSegment(sketch, "E298", {"start": v(-10, -37.5) * mm, "end": v(-10, -35.5) * mm, "construction": true});
            skLineSegment(sketch, "E299", {"start": v(-10, -37.5) * mm, "end": v(-12, -37.5) * mm, "construction": true});
            skLineSegment(sketch, "E300", {"start": v(-10, -58.5) * mm, "end": v(-10, -60.5) * mm, "construction": true});
            skLineSegment(sketch, "E301", {"start": v(-10, -37.5) * mm, "end": v(2.5, -37.5) * mm, "construction": true});
            skLineSegment(sketch, "E302", {"start": v(2.5, -37.5) * mm, "end": v(2.5, -58.5) * mm, "construction": true});
            skLineSegment(sketch, "E303", {"start": v(-10, -58.5) * mm, "end": v(2.5, -58.5) * mm, "construction": true});
            skCircle(sketch, "E304", {"center": v(-10, -37.5) * mm, "radius": 1.06 * mm});
            skCircle(sketch, "E305", {"center": v(2.5, -37.5) * mm, "radius": 1.06 * mm});
            skCircle(sketch, "E306", {"center": v(2.5, -58.5) * mm, "radius": 1.06 * mm});
            skCircle(sketch, "E307", {"center": v(-10, -58.5) * mm, "radius": 1.06 * mm});
            skSolve(sketch);
        }
        {
            var Q0;
            Q0=qSketchRegion(id+"F12",true);
            extrude(context, id + "F13", {"entities" : qUnion([Q0]), "depth" : 1 * mm});
        }
        {
            var Q0;
            Q0=makeQuery(id+"F13.opExtrude","CAP_FACE",FACE,{"disambiguationData":[OSD([sQuery(id+"F12.wireOp",EDGE,"E291.top"),sQuery(id+"F12.wireOp",EDGE,"E291.right"),sQuery(id+"F12.wireOp",EDGE,"E293.top"),sQuery(id+"F12.wireOp",EDGE,"E293.left"),sQuery(id+"F12.wireOp",EDGE,"E294.bottom"),sQuery(id+"F12.wireOp",EDGE,"E294.right"),sQuery(id+"F12.wireOp",EDGE,"E295.bottom"),sQuery(id+"F12.wireOp",EDGE,"E295.right"),sQuery(id+"F12.wireOp",EDGE,"E304"),sQuery(id+"F12.wireOp",EDGE,"E305"),sQuery(id+"F12.wireOp",EDGE,"E306"),sQuery(id+"F12.wireOp",EDGE,"E307")])],"isStart":false});
            var sketch = newSketch(context, id + "F14", { "sketchPlane" : qUnion([Q0])});
            skLineSegment(sketch, "E308.0.0", {"start": v(-12, -60.5) * mm, "end": v(12, -60.5) * mm, "construction": true});
            skLineSegment(sketch, "E308.0.1", {"start": v(12, -60.5) * mm, "end": v(12, -35.5) * mm, "construction": true});
            skLineSegment(sketch, "E308.0.2", {"start": v(12, -35.5) * mm, "end": v(-12, -35.5) * mm, "construction": true});
            skLineSegment(sketch, "E308.0.3", {"start": v(-12, -35.5) * mm, "end": v(-12, -60.5) * mm, "construction": true});
            skLineSegment(sketch, "E309", {"start": v(2.5, -37.5) * mm, "end": v(2.5, -58.5) * mm, "construction": true});
            skLineSegment(sketch, "E310", {"start": v(2.5, -37.5) * mm, "end": v(12, -37.5) * mm, "construction": true});
            skLineSegment(sketch, "E311", {"start": v(2.5, -58.5) * mm, "end": v(12, -58.5) * mm, "construction": true});
            skLineSegment(sketch, "E312", {"start": v(12, -48) * mm, "end": v(6, -48) * mm, "construction": true});
            skLineSegment(sketch, "E313.bottom", {"start": v(6, -37.5) * mm, "end": v(12, -37.5) * mm});
            skLineSegment(sketch, "E313.top", {"start": v(6, -58.5) * mm, "end": v(12, -58.5) * mm});
            skLineSegment(sketch, "E313.left", {"start": v(6, -37.5) * mm, "end": v(6, -58.5) * mm});
            skLineSegment(sketch, "E313.right", {"start": v(12, -37.5) * mm, "end": v(12, -58.5) * mm});
            skSolve(sketch);
        }
        {
            var Q0;
            Q0=qSketchRegion(id+"F14",true);
            extrude(context, id + "F15", {"entities" : qUnion([Q0]), "operationType" : NewBodyOperationType.ADD, "depth" : 3.75 * mm});
        }
        {
            var Q0;
            Q0=makeQuery(id+"F13.opExtrude","CAP_FACE",FACE,{"disambiguationData":[OSD([sQuery(id+"F12.wireOp",EDGE,"E291.top"),sQuery(id+"F12.wireOp",EDGE,"E291.right"),sQuery(id+"F12.wireOp",EDGE,"E293.top"),sQuery(id+"F12.wireOp",EDGE,"E293.left"),sQuery(id+"F12.wireOp",EDGE,"E294.bottom"),sQuery(id+"F12.wireOp",EDGE,"E294.right"),sQuery(id+"F12.wireOp",EDGE,"E295.bottom"),sQuery(id+"F12.wireOp",EDGE,"E295.right"),sQuery(id+"F12.wireOp",EDGE,"E304"),sQuery(id+"F12.wireOp",EDGE,"E305"),sQuery(id+"F12.wireOp",EDGE,"E306"),sQuery(id+"F12.wireOp",EDGE,"E307")])],"isStart":true});
            var sketch = newSketch(context, id + "F16", { "sketchPlane" : qUnion([Q0])});
            skLineSegment(sketch, "E314.0.0", {"start": v(-12, -60.5) * mm, "end": v(12, -60.5) * mm, "construction": true});
            skLineSegment(sketch, "E314.0.1", {"start": v(12, -60.5) * mm, "end": v(12, -35.5) * mm, "construction": true});
            skLineSegment(sketch, "E314.0.2", {"start": v(12, -35.5) * mm, "end": v(-12, -35.5) * mm, "construction": true});
            skLineSegment(sketch, "E314.0.3", {"start": v(-12, -35.5) * mm, "end": v(-12, -60.5) * mm, "construction": true});
            skLineSegment(sketch, "E315", {"start": v(-12, -48) * mm, "end": v(-6.5, -48) * mm, "construction": true});
            skLineSegment(sketch, "E316", {"start": v(-6.5, -48) * mm, "end": v(-6.5, -52) * mm});
            skLineSegment(sketch, "E317", {"start": v(-6.5, -52) * mm, "end": v(1.5, -52) * mm});
            skLineSegment(sketch, "E318", {"start": v(1.5, -52) * mm, "end": v(1.5, -48) * mm});
            skLineSegment(sketch, "E319", {"start": v(1.5, -52) * mm, "end": v(-2.5, -52) * mm, "construction": true});
            skLineSegment(sketch, "E320", {"start": v(1.5, -52) * mm, "end": v(-2.5, -48) * mm, "construction": true});
            skLineSegment(sketch, "E321", {"start": v(-2.5, -48) * mm, "end": v(-6.5, -44) * mm, "construction": true});
            skLineSegment(sketch, "E322", {"start": v(-6.5, -48) * mm, "end": v(-6.5, -44) * mm});
            skLineSegment(sketch, "E323", {"start": v(-6.5, -44) * mm, "end": v(1.5, -44) * mm});
            skLineSegment(sketch, "E324", {"start": v(1.5, -44) * mm, "end": v(1.5, -48) * mm});
            skSolve(sketch);
        }
        {
            var Q0;
            Q0=makeQuery(id+"F16.imprint","IMPRINT",FACE,{"disambiguationData":[TD([[makeQuery(id+"F16.imprint","IMPRINT",EDGE,{"derivedFrom":sQuery(id+"F16.wireOp",EDGE,"E316")}),1.0]])]});
            extrude(context, id + "F17", {"entities" : qUnion([Q0]), "operationType" : NewBodyOperationType.ADD, "depth" : 4.5 * mm});
        }
    });
